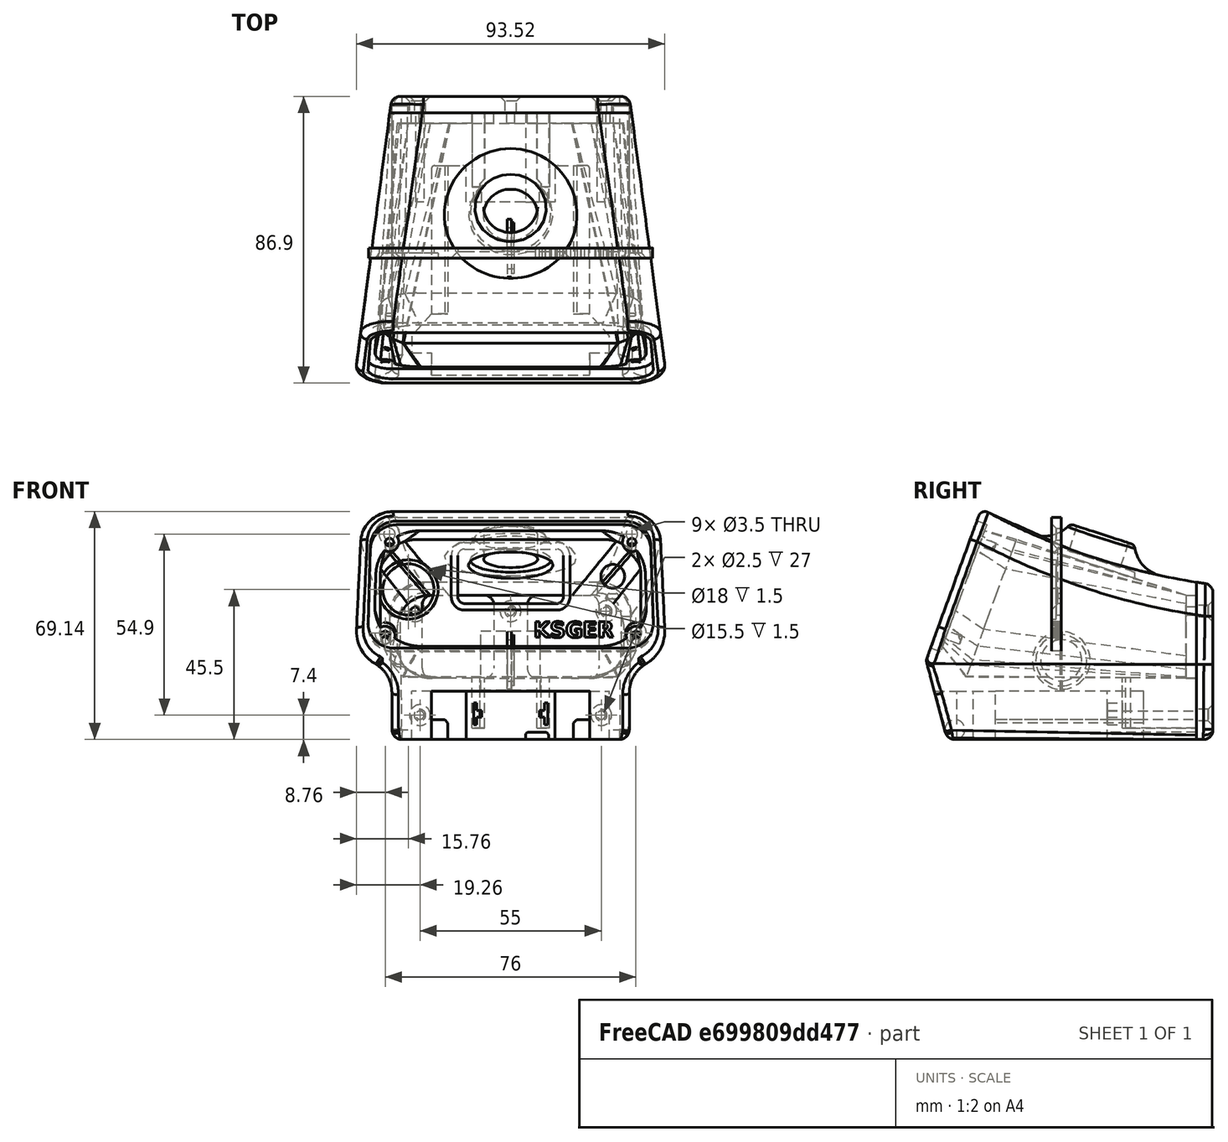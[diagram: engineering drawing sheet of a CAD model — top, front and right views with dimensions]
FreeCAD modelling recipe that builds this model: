
FCSTD DOCUMENT  (FreeCAD 2022.709R28846 (Git))
Label: solder_station5_snap_name
License: All rights reserved
LicenseURL: http://en.wikipedia.org/wiki/All_rights_reserved
objects: Sketcher::SketchObject×22, PartDesign::Pocket×12, Part::FeaturePython×6, PartDesign::Fillet×6, App::DocumentObjectGroup×4, PartDesign::Body×4, Mesh::Feature×4, PartDesign::Chamfer×3, PartDesign::FeatureBase×2, PartDesign::Pad×2, PartDesign::Revolution×2, Spreadsheet::Sheet×1, Part::Plane×1, Part::Loft×1, Part::Extrusion×1, Part::MultiCommon×1, Part::Box×1, PartDesign::SubtractiveLoft×1, PartDesign::Groove×1, Part::Part2DObjectPython×1, +2 more types
note: 124 computed .brp shape members not serialized (recipe doc carries the construction recipe); baked Part::Feature solids carry a one-line shape summary decoded from their .brp

FEATURE [Sketcher::SketchObject] Sketch  label="RearSupport"
  ArcFitTolerance = 0
  AttachmentOffset = pos=(0,0,-37.8) rot=(0,0,1;0rad)
  AttachmentSupport = -> [XZ_Plane005]
  FullyConstrained = true
  MapMode = 5
  Placement = pos=(0,37.8,8.4e-15) rot=(1,0,0;1.5708rad)
  Support = -> [XZ_Plane005]
  TreeRank = 0
  expr: AttachmentOffset.Base.z = -<<param>>.mid_depth / 2 + <<param>>.wall
  expr: Constraints[24] = 3
  expr: Constraints[37] = <<param>>.bottom_height
  expr: Constraints[38] = <<param>>.floor
  expr: Constraints[39] = <<param>>.rear_height - <<param>>.wall
  expr: Constraints[47] = <<param>>.reart_screw_width2
  expr: Constraints[48] = <<param>>.rear_screw_width1
  expr: Constraints[49] = <<param>>.screw_hole
  expr: Constraints[50] = <<param>>.rear_screw_height
  expr: Constraints[51] = <<param>>.rear_screw_height
  expr: Constraints[52] = <<param>>.rear_screw_offset
  sketch-geometry (22):
    g0: LineSegment StartX=-23.8 StartY=19.8 StartZ=0 EndX=-8.1 EndY=19.8 EndZ=0
    g1: LineSegment StartX=26.8 StartY=16.8 StartZ=0 EndX=26.8 EndY=-2.4 EndZ=0
    g2: LineSegment StartX=23.8 StartY=-5.4 StartZ=0 EndX=8.1 EndY=-5.4 EndZ=0
    g3: LineSegment StartX=-26.8 StartY=-2.4 StartZ=0 EndX=-26.8 EndY=16.8 EndZ=0
    g4: LineSegment StartX=-5.1 StartY=16.8 StartZ=0 EndX=-5.1 EndY=-2.4 EndZ=0
    g5: LineSegment StartX=5.1 StartY=16.8 StartZ=0 EndX=5.1 EndY=-2.4 EndZ=0
    g6: LineSegment StartX=8.1 StartY=19.8 StartZ=0 EndX=23.8 EndY=19.8 EndZ=0
    g7: LineSegment StartX=-8.1 StartY=-5.4 StartZ=0 EndX=-23.8 EndY=-5.4 EndZ=0
    g8: ArcOfCircle CenterX=-8.1 CenterY=16.8 CenterZ=0 NormalX=0 NormalY=0 NormalZ=1 AngleXU=0 Radius=3 StartAngle=0 EndAngle=1.5708
    g9: ArcOfCircle CenterX=8.1 CenterY=16.8 CenterZ=0 NormalX=0 NormalY=0 NormalZ=1 AngleXU=0 Radius=3 StartAngle=1.5708 EndAngle=3.14159
    g10: ArcOfCircle CenterX=-8.1 CenterY=-2.4 CenterZ=0 NormalX=0 NormalY=0 NormalZ=1 AngleXU=0 Radius=3 StartAngle=4.71239 EndAngle=6.28319
    g11: ArcOfCircle CenterX=8.1 CenterY=-2.4 CenterZ=0 NormalX=0 NormalY=0 NormalZ=1 AngleXU=0 Radius=3 StartAngle=3.14159 EndAngle=4.71239
    g12: ArcOfCircle CenterX=-23.8 CenterY=16.8 CenterZ=0 NormalX=0 NormalY=0 NormalZ=1 AngleXU=0 Radius=3 StartAngle=1.5708 EndAngle=3.14159
    g13: ArcOfCircle CenterX=-23.8 CenterY=-2.4 CenterZ=0 NormalX=0 NormalY=0 NormalZ=1 AngleXU=0 Radius=3 StartAngle=3.14159 EndAngle=4.71239
    g14: ArcOfCircle CenterX=23.8 CenterY=16.8 CenterZ=0 NormalX=0 NormalY=0 NormalZ=1 AngleXU=0 Radius=3 StartAngle=3e-16 EndAngle=1.5708
    g15: ArcOfCircle CenterX=23.8 CenterY=-2.4 CenterZ=0 NormalX=0 NormalY=0 NormalZ=1 AngleXU=0 Radius=3 StartAngle=4.71239 EndAngle=6.28319
    g16: Circle [constr] CenterX=0 CenterY=-24 CenterZ=0 NormalX=0 NormalY=0 NormalZ=1 AngleXU=0 Radius=3
    g17: Circle CenterX=0 CenterY=14.9 CenterZ=0 NormalX=0 NormalY=0 NormalZ=1 AngleXU=0 Radius=1.25
    g18: Circle CenterX=-29 CenterY=14.9 CenterZ=0 NormalX=0 NormalY=0 NormalZ=1 AngleXU=0 Radius=1.25
    g19: Circle [constr] CenterX=-27.5 CenterY=-16.6 CenterZ=0 NormalX=0 NormalY=0 NormalZ=1 AngleXU=0 Radius=1.25
    g20: Circle [constr] CenterX=27.5 CenterY=-16.6 CenterZ=0 NormalX=0 NormalY=0 NormalZ=1 AngleXU=0 Radius=1.25
    g21: Circle CenterX=29 CenterY=14.9 CenterZ=0 NormalX=0 NormalY=0 NormalZ=1 AngleXU=0 Radius=1.25
  constraints (53):
    c: Horizontal(g0)
    c: Horizontal(g2)
    c: Vertical(g1)
    c: Vertical(g3)
    c: Vertical(g4)
    c: Vertical(g5)
    c: Tangent(g0,g6)
    c: Tangent(g2,g7)
    c: Tangent(g0,g8) = 1.5708
    c: Tangent(g4,g8) = 1.5708
    c: Tangent(g5,g9) = -1.5708
    c: Tangent(g6,g9) = 1.5708
    c: Tangent(g7,g10) = 1.5708
    c: Tangent(g4,g10) = 1.5708
    c: Tangent(g5,g11) = -1.5708
    c: Tangent(g2,g11) = 1.5708
    c: Tangent(g0,g12) = 1.5708
    c: Tangent(g3,g12) = 1.5708
    c: Tangent(g3,g13) = 1.5708
    c: Tangent(g7,g13) = 1.5708
    c: Tangent(g6,g14) = 1.5708
    c: Tangent(g1,g14) = 1.5708
    c: Tangent(g1,g15) = 1.5708
    c: Tangent(g2,g15) = 1.5708
    c: Radius(g9) = 3
    c: Equal(g12,g13)
    c: Equal(g13,g10)
    c: Equal(g10,g8)
    c: Equal(g11,g15)
    c: Equal(g15,g14)
    c: Equal(g14,g9)
    c: DistanceX(g4,g-1) = 5.1
    c: DistanceX(g5,g1) = 21.7
    c: Symmetric(g4,g5,g-2)
    c: Equal(g7,g2)
    c: PointOnObject(g16,g-2)
    c: Radius(g16) = 3
    c: DistanceY(g16,g-1) = 24
    c: DistanceY(g16,g2) = 18.6
    c: DistanceY(g16,g6) = 43.8
    c: PointOnObject(g17,g-2)
    c: Equal(g21,g18)
    c: Equal(g18,g19)
    c: Equal(g19,g20)
    c: Equal(g18,g17)
    c: Symmetric(g20,g19,g-2)
    c: Symmetric(g18,g21,g-2)
    c: DistanceX(g19,g20) = 55
    c: DistanceX(g18,g21) = 58
    c: Diameter(g19) = 2.5
    c: DistanceY(g20,g21) = 31.5
    c: DistanceY(g20,g17) = 31.5
    c: DistanceY(g16,g19) = 7.4
FEATURE [Spreadsheet::Sheet] Spreadsheet  label="param"
  PythonMode = false
  ShowCells = 0
  TreeRank = 0
  cells = A1=Body; B2=top_depth; C2(top_depth)=70; B3=mid_depth; C3(mid_depth)=82; D3=half is rear reference; B4=bottom_depth; C4(bottom_depth)=75; B6=bottom_width; C6(bottom_width)=72; B7=bottom_height; C7(bottom_height)=24; B8=bottom_angle; C8(bottom_angle)=15; B10=rear_width; C10(rear_width)=72; B11=rear_height; C11(rear_height)=47; F11=41; B13=mid_width; C13(mid_width)=80; B14=mid_height; C14(mid_height)=56; F14=50; B16=front_width1; C16(front_width1)=92; D16=@top; E16=upper; F16=91; B17=front_width2; C17(front_width2)=95; D17=@mid; E17=lower; F17=94; B18=front_height; C18(front_height)=70; F18=64; B19=front_angle; C19(front_angle)=20; B21=wall; C21(wall)=3.2; B22=radius_big; C22(radius_big)=10; B23=radius_small; C23(radius_small)=3; B24=arch; C24(arch)=200; A26=Button; B27=button_offset; C27(button_offset)=10; B28=button_inside_dia; C28(button_inside_dia)=20; B29=button_outside_dia; C29(button_outside_dia)=22; B30=button_height; C30(button_height)=30.6; F30=26; B31=button_extension; C31(button_extension)=8; B32=button_fillet; C32(button_fillet)=12; B33=button_angle; C33(button_angle)=-18; F33=-17; B34=button_hole; C34(button_hole)=16.4; B35=button_hole_center; C35(button_hole_center)=-0.5; A37=Battery Cuts; B38=batt_carveout; C38(batt_carveout)=14.6; B39=batt_rail; C39(batt_rail)=6; B40=batt_rail_length; C40(batt_rail_length)=45; A42=Terminals; B43=terminal_height; C43(terminal_height)=6.6; B44=terminal_thickness; C44(terminal_thickness)=1; B45=terminal_seperation; C45(terminal_seperation)=21.5; B46=terminal_offset; C46(terminal_offset)=4.5; B47=terminal_depth; C47(terminal_depth)=22.5; A49=Box Interior; B50=floor; C50(floor)=18.6; B51=rear_inside_width; C51(rear_inside_width)==C10 - C21; D51=calc; B52=rear_inside_height; C52(rear_inside_height)==C11 - C21; D52=calc; B53=mid_inside_width; C53(mid_inside_width)==C13; D53=calc; B54=mid_inside_height; C54(mid_inside_height)==C14 + 7; D54=calc; F54=6; B55=front_inside_width1; C55(front_inside_width1)==C62 - C58 * 2; D55=calc; E55=upper; B56=front_inside_width2; C56(front_inside_width2)==C63 - C58 * 2; D56=calc; E56=lower; B57=front_inside_height; C57(front_inside_height)==C64 - C59 * 2; D57=calc; B58=front_width_lip_width; C58(front_width_lip_width)=3; B59=front_inside_lip_height; C59(front_inside_lip_height)=2; A61=Face; B62=face_width1; C62(face_width1)==84 + 1; B63=face_width2; C63(face_width2)==85.5 + 1; B64=face_height; C64(face_height)=41; F64=35; B65=face_thickness; C65(face_thickness)=3; B66=face_radius; C66(face_radius)=8; B67=face_offset; C67(face_offset)=2.8; F67=2.8; A69=Screws; B70=screw_hole; C70(screw_hole)=2.5; B72=front_screw_width1; C72(front_screw_width1)=73.5; D72=upper; B73=front_screw_width2; C73(front_screw_width2)=76; D73=lower; B74=front_screw_height; C74(front_screw_height)=30; F74=24; B75=front_screw_offset; C75(front_screw_offset)=5.5; B77=rear_screw_width1; C77(rear_screw_width1)=58; B78=reart_screw_width2; C78(reart_screw_width2)=55; B79=rear_screw_height; C79(rear_screw_height)=31.5; F79=25.5; B80=rear_screw_offset; C80(rear_screw_offset)=7.4; A82=Back; B83=back_thickness; C83(back_thickness)=5
FEATURE [Sketcher::SketchObject] Sketch008  label="SketchButtonHole"
  ArcFitTolerance = 0
  AttachmentOffset = pos=(0,-0.5,30.6) rot=(1,0,0;-0.314159rad)
  AttachmentSupport = -> [XY_Plane005]
  FullyConstrained = true
  MapMode = 5
  Placement = pos=(0,-0.5,30.6) rot=(1,0,0;5.96903rad)
  Support = -> [XY_Plane005]
  TreeRank = 0
  expr: AttachmentOffset.Base.y = <<param>>.button_hole_center
  expr: AttachmentOffset.Base.z = <<param>>.button_height
  expr: AttachmentOffset.Rotation.Angle = <<param>>.button_angle
  expr: Constraints[0] = <<param>>.button_hole
  expr: Constraints[2] = <<param>>.button_offset
  sketch-geometry (1):
    g0: Circle CenterX=0 CenterY=10 CenterZ=0 NormalX=0 NormalY=0 NormalZ=1 AngleXU=0 Radius=8.2
  constraints (3):
    c: Diameter(g0) = 16.4
    c: PointOnObject(g0,g-2)
    c: DistanceY(g-1,g0) = 10
FEATURE [Sketcher::SketchObject] Sketch012  label="SketchSide"
  ArcFitTolerance = 0
  AttachmentOffset = pos=(2.5,0,0) rot=(0,0,1;0rad)
  AttachmentSupport = -> [YZ_Plane006]
  FullyConstrained = true
  MapMode = 5
  Placement = pos=(6e-16,2.5,-6e-16) rot=(0.57735,0.57735,0.57735;2.0944rad)
  Support = -> [YZ_Plane006]
  TreeRank = 0
  expr: AttachmentOffset.Base.x = <<param>>.back_thickness / 2
  expr: Constraints[14] = <<param>>.bottom_height
  expr: Constraints[15] = <<param>>.radius_small
  expr: Constraints[16] = 90 - <<param>>.bottom_angle
  expr: Constraints[17] = 90 - <<param>>.front_angle
  expr: Constraints[21] = <<param>>.front_height
  expr: Constraints[4] = <<param>>.rear_height - <<param>>.bottom_height
  expr: Constraints[5] = <<param>>.arch
  expr: Constraints[6] = <<param>>.mid_depth + <<param>>.back_thickness
  sketch-geometry (7):
    g0: LineSegment StartX=43.5 StartY=0 StartZ=0 EndX=43.5 EndY=23 EndZ=0
    g1: LineSegment StartX=-43.5 StartY=0 StartZ=0 EndX=-26.7574 EndY=46 EndZ=0
    g2: ArcOfCircle CenterX=69.5235 CenterY=221.3 CenterZ=0 NormalX=0 NormalY=0 NormalZ=1 AngleXU=0 Radius=200 StartAngle=4.21013 EndAngle=4.5819
    g3: LineSegment StartX=-43.5 StartY=0 StartZ=0 EndX=-37.665 EndY=-21.7765 EndZ=0
    g4: LineSegment StartX=-34.7673 StartY=-24 StartZ=0 EndX=43.5 EndY=-24 EndZ=0
    g5: LineSegment StartX=43.5 StartY=-24 StartZ=0 EndX=43.5 EndY=0 EndZ=0
    g6: ArcOfCircle CenterX=-34.7672 CenterY=-21 CenterZ=0 NormalX=0 NormalY=0 NormalZ=1 AngleXU=0 Radius=3 StartAngle=3.4034 EndAngle=4.71238
  constraints (22):
    c: PointOnObject(g1,g-1)
    c: Vertical(g0)
    c: Coincident(g2,g0)
    c: Symmetric(g1,g0,g-2)
    c: DistanceY(g0,g0) = 23
    c: Radius(g2) = 200
    c: DistanceX(g1,g0) = 87
    c: Horizontal(g4)
    c: Coincident(g5,g4)
    c: Vertical(g5)
    c: Coincident(g6,g3)
    c: Coincident(g6,g4)
    c: Tangent(g6,g4)
    c: Tangent(g6,g3)
    c: DistanceY(g4,g-1) = 24
    c: Radius(g6) = 3
    c: Angle(g3,g-1) = 1.309
    c: Angle(g-1,g1) = 1.22173
    c: Coincident(g3,g1)
    c: Coincident(g5,g0)
    c: Coincident(g2,g1)
    c: DistanceY(g4,g1) = 70
FEATURE [Sketcher::SketchObject] Sketch018  label="SketchBat1"
  ArcFitTolerance = 0
  AttachmentOffset = pos=(0,0,-24) rot=(0,0,1;0rad)
  AttachmentSupport = -> [XY_Plane005]
  FullyConstrained = true
  MapMode = 5
  Placement = pos=(0,0,-24) rot=(0,0,1;0rad)
  Support = -> [XY_Plane005]
  TreeRank = 0
  expr: AttachmentOffset.Base.z = -<<param>>.bottom_height
  expr: Constraints[63] = <<param>>.batt_rail_length
  expr: Constraints[64] = <<param>>.mid_depth / 2
  sketch-geometry (21):
    g0: LineSegment StartX=-24 StartY=-41.7082 StartZ=0 EndX=24 EndY=-41.7082 EndZ=0
    g1: LineSegment StartX=24 StartY=-41.7082 StartZ=0 EndX=24 EndY=-31.7082 EndZ=0
    g2: LineSegment StartX=24 StartY=-31.7082 StartZ=0 EndX=30 EndY=-31.7082 EndZ=0
    g3: LineSegment StartX=30 StartY=-31.7082 StartZ=0 EndX=30 EndY=-26.7082 EndZ=0
    g4: LineSegment StartX=30 StartY=-26.7082 StartZ=0 EndX=24 EndY=-20 EndZ=0
    g5: LineSegment StartX=24 StartY=-20 StartZ=0 EndX=24 EndY=24 EndZ=0
    g6: LineSegment StartX=13.5 StartY=24 StartZ=0 EndX=13.5 EndY=14 EndZ=0
    g7: LineSegment StartX=13.5 StartY=14 StartZ=0 EndX=-13.5 EndY=14 EndZ=0
    g8: LineSegment StartX=-13.5 StartY=14 StartZ=0 EndX=-13.5 EndY=24 EndZ=0
    g9: LineSegment StartX=-24 StartY=24 StartZ=0 EndX=-24 EndY=-20 EndZ=0
    g10: LineSegment StartX=-24 StartY=-20 StartZ=0 EndX=-30 EndY=-26.7082 EndZ=0
    g11: LineSegment StartX=-30 StartY=-26.7082 StartZ=0 EndX=-30 EndY=-31.7082 EndZ=0
    g12: LineSegment StartX=-30 StartY=-31.7082 StartZ=0 EndX=-24 EndY=-31.7082 EndZ=0
    g13: LineSegment StartX=-24 StartY=-31.7082 StartZ=0 EndX=-24 EndY=-41.7082 EndZ=0
    g14: Circle [constr] CenterX=0 CenterY=41 CenterZ=0 NormalX=0 NormalY=0 NormalZ=1 AngleXU=0 Radius=4
    g15: ArcOfCircle CenterX=-14.5 CenterY=24 CenterZ=0 NormalX=0 NormalY=0 NormalZ=1 AngleXU=0 Radius=1 StartAngle=6.28318 EndAngle=7.85399
    g16: LineSegment StartX=-23 StartY=25 StartZ=0 EndX=-14.5 EndY=25 EndZ=0
    g17: LineSegment StartX=14.5 StartY=25 StartZ=0 EndX=23 EndY=25 EndZ=0
    g18: ArcOfCircle CenterX=-23 CenterY=24 CenterZ=0 NormalX=0 NormalY=0 NormalZ=1 AngleXU=0 Radius=1 StartAngle=1.57079 EndAngle=3.1416
    g19: ArcOfCircle CenterX=14.5 CenterY=24 CenterZ=0 NormalX=0 NormalY=0 NormalZ=1 AngleXU=0 Radius=1 StartAngle=1.5708 EndAngle=3.14159
    g20: ArcOfCircle CenterX=23 CenterY=24 CenterZ=0 NormalX=0 NormalY=0 NormalZ=1 AngleXU=0 Radius=1.00001 StartAngle=2.75124e-06 EndAngle=1.5708
  constraints (65):
    c: Horizontal(g0)
    c: Coincident(g1,g0)
    c: Vertical(g1)
    c: Coincident(g2,g1)
    c: Horizontal(g2)
    c: Coincident(g3,g2)
    c: Coincident(g3,g4)
    c: Vertical(g5)
    c: Coincident(g6,g7)
    c: Coincident(g7,g8)
    c: Vertical(g8)
    c: Vertical(g9)
    c: Coincident(g10,g11)
    c: Vertical(g11)
    c: Coincident(g11,g12)
    c: Horizontal(g12)
    c: Coincident(g12,g13)
    c: Equal(g6,g8)
    c: Equal(g5,g9)
    c: Equal(g4,g10)
    c: Equal(g3,g11)
    c: Equal(g12,g2)
    c: Equal(g1,g13)
    c: Coincident(g13,g0)
    c: Vertical(g13)
    c: DistanceX(g7,g7) = 27
    c: Symmetric(g7,g6,g-2)
    c: Distance(g4) = 9
    c: Vertical(g3)
    c: DistanceY(g3,g3) = 5
    c: DistanceX(g2,g2) = 6
    c: DistanceY(g1,g1) = 10
    c: DistanceX(g0,g0) = 48
    c: PointOnObject(g14,g-2)
    c: Coincident(g9,g10)
    c: Coincident(g5,g4)
    c: Coincident(g15,g8)
    c: Coincident(g16,g15)
    c: Tangent(g15,g8)
    c: Horizontal(g16)
    c: Horizontal(g17)
    c: DistanceX(g9,g5) = 48
    c: Symmetric(g4,g9,g-2)
    c: Equal(g16,g17)
    c: Coincident(g18,g9)
    c: Coincident(g18,g16)
    c: Equal(g18,g15)
    c: Tangent(g18,g16)
    c: Tangent(g18,g9)
    c: DistanceY(g6,g17) = 11
    c: Vertical(g6)
    c: Coincident(g19,g6)
    c: Coincident(g19,g17)
    c: Coincident(g20,g17)
    c: Coincident(g20,g5)
    c: Tangent(g20,g17)
    c: Tangent(g20,g5)
    c: Tangent(g19,g6)
    c: Tangent(g19,g17)
    c: Equal(g15,g19)
    c: Radius(g19) = 1
    c: Radius(g14) = 4
    c: DistanceY(g15,g14) = 16
    c: DistanceY(g9,g16) = 45
    c: DistanceY(g-1,g14) = 41
FEATURE [Sketcher::SketchObject] Sketch019  label="SketchBat2"
  ArcFitTolerance = 0
  AttachmentOffset = pos=(0,0,-25) rot=(0,0,1;0rad)
  AttachmentSupport = -> [XZ_Plane005]
  FullyConstrained = true
  MapMode = 5
  Placement = pos=(0,25,5.6e-15) rot=(1,0,0;1.5708rad)
  Support = -> [XZ_Plane005]
  TreeRank = 0
  expr: AttachmentOffset.Base.z = -<<param>>.mid_depth / 2 + 16
  expr: Constraints[17] = <<param>>.bottom_height
  expr: Constraints[18] = <<param>>.batt_rail
  expr: Constraints[19] = 48.01mm
  sketch-geometry (10):
    g0: LineSegment StartX=-24.005 StartY=-18 StartZ=0 EndX=-20.005 EndY=-18 EndZ=0
    g1: LineSegment StartX=-19.005 StartY=-24 StartZ=0 EndX=-24.005 EndY=-24 EndZ=0
    g2: LineSegment StartX=-24.005 StartY=-24 StartZ=0 EndX=-24.005 EndY=-18 EndZ=0
    g3: LineSegment StartX=24.005 StartY=-18 StartZ=0 EndX=20.005 EndY=-18 EndZ=0
    g4: LineSegment StartX=19.005 StartY=-24 StartZ=0 EndX=24.005 EndY=-24 EndZ=0
    g5: LineSegment StartX=24.005 StartY=-24 StartZ=0 EndX=24.005 EndY=-18 EndZ=0
    g6: LineSegment StartX=-19.005 StartY=-19 StartZ=0 EndX=-19.005 EndY=-24 EndZ=0
    g7: LineSegment StartX=19.005 StartY=-24 StartZ=0 EndX=19.005 EndY=-19 EndZ=0
    g8: LineSegment StartX=-20.005 StartY=-18 StartZ=0 EndX=-19.005 EndY=-19 EndZ=0
    g9: LineSegment StartX=19.005 StartY=-19 StartZ=0 EndX=20.005 EndY=-18 EndZ=0
  constraints (29):
    c: Coincident(g1,g2)
    c: Coincident(g2,g0)
    c: Horizontal(g0)
    c: Horizontal(g1)
    c: Vertical(g2)
    c: Coincident(g4,g5)
    c: Coincident(g5,g3)
    c: Horizontal(g3)
    c: Horizontal(g4)
    c: Vertical(g5)
    c: Coincident(g6,g1)
    c: Vertical(g6)
    c: Equal(g1,g4)
    c: Coincident(g7,g4)
    c: Vertical(g7)
    c: Equal(g6,g7)
    c: Symmetric(g1,g4,g-2)
    c: DistanceY(g1,g-1) = 24
    c: DistanceY(g4,g3) = 6
    c: DistanceX(g1,g4) = 48.01
    c: DistanceX(g4,g4) = 5
    c: Coincident(g8,g0)
    c: Coincident(g8,g6)
    c: Coincident(g9,g7)
    c: Coincident(g9,g3)
    c: Equal(g0,g3)
    c: Equal(g2,g5)
    c: DistanceX(g0,g0) = 4
    c: DistanceY(g1,g6) = 5
FEATURE [Sketcher::SketchObject] Sketch021  label="SketchButton"
  ArcFitTolerance = 0
  AttachmentOffset = pos=(10,30.6,0) rot=(0,0,1;-0.314159rad)
  AttachmentSupport = -> [YZ_Plane005]
  FullyConstrained = true
  MapMode = 5
  Placement = pos=(-4.6e-15,10,30.6) rot=(-0.506732,-0.697457,-0.506732;4.35963rad)
  Support = -> [YZ_Plane005]
  TreeRank = 0
  expr: AttachmentOffset.Base.x = <<param>>.button_offset
  expr: AttachmentOffset.Base.y = <<param>>.button_height
  expr: AttachmentOffset.Rotation.Angle = <<param>>.button_angle
  expr: Constraints[6] = <<param>>.button_extension
  expr: Constraints[7] = <<param>>.button_outside_dia / 2
  sketch-geometry (5):
    g0: LineSegment StartX=0 StartY=0 StartZ=0 EndX=0 EndY=8 EndZ=0
    g1: LineSegment StartX=0 StartY=8 StartZ=0 EndX=9 EndY=8 EndZ=0
    g2: LineSegment StartX=0 StartY=0 StartZ=0 EndX=11 EndY=0 EndZ=0
    g3: LineSegment StartX=11 StartY=0 StartZ=0 EndX=11 EndY=6 EndZ=0
    g4: ArcOfCircle CenterX=9 CenterY=6 CenterZ=0 NormalX=0 NormalY=0 NormalZ=1 AngleXU=0 Radius=2 StartAngle=1e-16 EndAngle=1.5708
  constraints (13):
    c: Coincident(g0,g-1)
    c: PointOnObject(g0,g-2)
    c: Coincident(g1,g0)
    c: Horizontal(g1)
    c: Coincident(g2,g0)
    c: Horizontal(g2)
    c: DistanceY(g0,g0) = 8
    c: DistanceX(g2,g2) = 11
    c: Coincident(g3,g2)
    c: Vertical(g3)
    c: Radius(g4) = 2
    c: Tangent(g4,g1) = 1.5708
    c: Tangent(g4,g3) = -1.5708
FEATURE [Sketcher::SketchObject] Sketch022  label="SketchRearInside"
  ArcFitTolerance = 0
  AttachmentOffset = pos=(0,0,-37.8) rot=(0,0,1;0rad)
  AttachmentSupport = -> [XZ_Plane005]
  FullyConstrained = true
  MapMode = 5
  Placement = pos=(0,37.8,8.4e-15) rot=(1,0,0;1.5708rad)
  Support = -> [XZ_Plane005]
  TreeRank = 0
  expr: AttachmentOffset.Base.z = -<<param>>.mid_depth / 2 + <<param>>.wall
  expr: Constraints[12] = <<param>>.radius_big
  expr: Constraints[18] = <<param>>.rear_inside_width
  expr: Constraints[26] = <<param>>.bottom_height
  expr: Constraints[27] = <<param>>.rear_inside_height
  expr: Constraints[29] = <<param>>.floor
  sketch-geometry (9):
    g0: LineSegment StartX=-34.4 StartY=9.80003 StartZ=0 EndX=-34.4 EndY=4.59997 EndZ=0
    g1: LineSegment StartX=-24.4 StartY=-5.4 StartZ=0 EndX=24.4 EndY=-5.4 EndZ=0
    g2: LineSegment StartX=34.4 StartY=4.59997 StartZ=0 EndX=34.4 EndY=9.80003 EndZ=0
    g3: LineSegment StartX=-24.4 StartY=19.8 StartZ=0 EndX=24.4 EndY=19.8 EndZ=0
    g4: ArcOfCircle CenterX=24.4 CenterY=9.8 CenterZ=0 NormalX=0 NormalY=0 NormalZ=1 AngleXU=0 Radius=10 StartAngle=3.49027e-06 EndAngle=1.57079
    g5: ArcOfCircle CenterX=24.4 CenterY=4.6 CenterZ=0 NormalX=0 NormalY=0 NormalZ=1 AngleXU=0 Radius=10 StartAngle=4.71239 EndAngle=6.28318
    g6: ArcOfCircle CenterX=-24.4 CenterY=9.8 CenterZ=0 NormalX=0 NormalY=0 NormalZ=1 AngleXU=0 Radius=10 StartAngle=1.5708 EndAngle=3.14159
    g7: ArcOfCircle CenterX=-24.4 CenterY=4.6 CenterZ=0 NormalX=0 NormalY=0 NormalZ=1 AngleXU=0 Radius=10 StartAngle=3.1416 EndAngle=4.71239
    g8: Circle [constr] CenterX=0 CenterY=-24 CenterZ=0 NormalX=0 NormalY=0 NormalZ=1 AngleXU=0 Radius=3
  constraints (30):
    c: Vertical(g0)
    c: Horizontal(g1)
    c: Vertical(g2)
    c: Horizontal(g3)
    c: Equal(g3,g1)
    c: Equal(g0,g2)
    c: Coincident(g4,g3)
    c: Coincident(g4,g2)
    c: Coincident(g5,g2)
    c: Coincident(g5,g1)
    c: Coincident(g6,g0)
    c: Coincident(g6,g3)
    c: Radius(g6) = 10
    c: Equal(g6,g4)
    c: Equal(g4,g5)
    c: Coincident(g7,g1)
    c: Coincident(g7,g0)
    c: Equal(g5,g7)
    c: DistanceX(g0,g2) = 68.8
    c: Symmetric(g0,g2,g-2)
    c: Tangent(g4,g2)
    c: Tangent(g4,g3)
    c: Tangent(g5,g2)
    c: Tangent(g5,g1)
    c: Tangent(g6,g3)
    c: PointOnObject(g8,g-2)
    c: DistanceY(g8,g-1) = 24
    c: DistanceY(g8,g3) = 43.8
    c: Radius(g8) = 3
    c: DistanceY(g8,g1) = 18.6
FEATURE [Sketcher::SketchObject] Sketch024  label="SketchFaceCut"
  ArcFitTolerance = 0
  AttachmentOffset = pos=(0,0,37.6) rot=(1,0,0;-0.349066rad)
  AttachmentSupport = -> [XZ_Plane005]
  FullyConstrained = true
  MapMode = 5
  Placement = pos=(0,-37.6,-8.3e-15) rot=(-1,0,0;5.06145rad)
  Support = -> [XZ_Plane005]
  TreeRank = 0
  expr: AttachmentOffset.Base.z = <<param>>.mid_depth / 2 - <<param>>.face_thickness - 0.4
  expr: AttachmentOffset.Rotation.Angle = -<<param>>.front_angle
  expr: Constraints[13] = <<param>>.face_radius
  expr: Constraints[22] = <<param>>.face_width1
  expr: Constraints[23] = <<param>>.face_width2
  expr: Constraints[24] = <<param>>.face_offset
  expr: Constraints[25] = <<param>>.face_height
  sketch-geometry (8):
    g0: LineSegment StartX=-34.5035 StartY=43.8 StartZ=0 EndX=34.5037 EndY=43.8 EndZ=0
    g1: LineSegment StartX=42.5001 StartY=36.0399 StartZ=0 EndX=43.25 EndY=11.0399 EndZ=0
    g2: LineSegment StartX=35.2536 StartY=2.8 StartZ=0 EndX=-35.2536 EndY=2.8 EndZ=0
    g3: LineSegment StartX=-43.25 StartY=11.0399 StartZ=0 EndX=-42.4999 EndY=36.0399 EndZ=0
    g4: ArcOfCircle CenterX=34.5037 CenterY=35.8 CenterZ=0 NormalX=0 NormalY=0 NormalZ=1 AngleXU=0 Radius=8 StartAngle=0.0299879 EndAngle=1.5708
    g5: ArcOfCircle CenterX=35.2536 CenterY=10.8 CenterZ=0 NormalX=0 NormalY=0 NormalZ=1 AngleXU=0 Radius=8 StartAngle=4.71239 EndAngle=6.31317
    g6: ArcOfCircle CenterX=-34.5035 CenterY=35.8 CenterZ=0 NormalX=0 NormalY=0 NormalZ=1 AngleXU=0 Radius=8 StartAngle=1.5708 EndAngle=3.1116
    g7: ArcOfCircle CenterX=-35.2536 CenterY=10.8 CenterZ=0 NormalX=0 NormalY=0 NormalZ=1 AngleXU=0 Radius=8 StartAngle=3.1116 EndAngle=4.71239
  constraints (27):
    c: Horizontal(g0)
    c: Coincident(g4,g0)
    c: Coincident(g4,g1)
    c: Coincident(g5,g1)
    c: Coincident(g5,g2)
    c: Coincident(g6,g0)
    c: Coincident(g6,g3)
    c: Coincident(g7,g3)
    c: Coincident(g7,g2)
    c: Equal(g1,g3)
    c: Equal(g4,g6)
    c: Equal(g6,g7)
    c: Equal(g7,g5)
    c: Radius(g4) = 8
    c: Tangent(g6,g3)
    c: Tangent(g7,g3)
    c: Tangent(g7,g2)
    c: Tangent(g6,g0)
    c: Tangent(g4,g0)
    c: Tangent(g4,g1)
    c: Tangent(g5,g1)
    c: Tangent(g5,g2)
    c: DistanceX(g3,g1) = 85
    c: DistanceX(g3,g1) = 86.5
    c: DistanceY(g-1,g2) = 2.8
    c: DistanceY(g2,g0) = 41
    c: Symmetric(g2,g2,g-2)
FEATURE [Sketcher::SketchObject] Sketch025  label="SketchMidInside"
  ArcFitTolerance = 0
  AttachmentOffset = pos=(0,0,27) rot=(1,0,0;-0.349066rad)
  AttachmentSupport = -> [XZ_Plane005]
  FullyConstrained = true
  MapMode = 5
  Placement = pos=(0,-27,-6e-15) rot=(-1,0,0;5.06145rad)
  Support = -> [XZ_Plane005]
  TreeRank = 0
  expr: AttachmentOffset.Base.z = <<param>>.mid_depth / 2 - 14
  expr: AttachmentOffset.Rotation.Angle = -<<param>>.front_angle
  expr: Constraints[10] = <<param>>.radius_big + 1
  expr: Constraints[11] = <<param>>.floor
  expr: Constraints[12] = Spreadsheet.mid_inside_width - 1
  expr: Constraints[14] = <<param>>.mid_inside_height
  expr: Constraints[23] = <<param>>.mid_width - 15
  expr: Constraints[4] = <<param>>.bottom_height
  sketch-geometry (9):
    g0: LineSegment StartX=-28.5 StartY=39 StartZ=0 EndX=28.5 EndY=39 EndZ=0
    g1: LineSegment StartX=39.5 StartY=28 StartZ=0 EndX=39.5 EndY=10 EndZ=0
    g2: LineSegment StartX=32.5 StartY=-5.4 StartZ=0 EndX=-32.5 EndY=-5.4 EndZ=0
    g3: LineSegment StartX=-39.5 StartY=10 StartZ=0 EndX=-39.5 EndY=28 EndZ=0
    g4: Circle [constr] CenterX=0 CenterY=-24 CenterZ=0 NormalX=0 NormalY=0 NormalZ=1 AngleXU=0 Radius=3
    g5: ArcOfCircle CenterX=-28.5 CenterY=28 CenterZ=0 NormalX=0 NormalY=0 NormalZ=1 AngleXU=0 Radius=11 StartAngle=1.5708 EndAngle=3.14159
    g6: ArcOfCircle CenterX=28.5 CenterY=28 CenterZ=0 NormalX=0 NormalY=0 NormalZ=1 AngleXU=0 Radius=11 StartAngle=0 EndAngle=1.5708
    g7: ArcOfCircle CenterX=-15.553 CenterY=11.5941 CenterZ=0 NormalX=0 NormalY=0 NormalZ=1 AngleXU=0 Radius=24 StartAngle=3.20806 EndAngle=3.92838
    g8: ArcOfCircle CenterX=15.553 CenterY=11.5941 CenterZ=0 NormalX=0 NormalY=0 NormalZ=1 AngleXU=0 Radius=24 StartAngle=5.4964 EndAngle=6.21672
  constraints (25):
    c: Vertical(g1)
    c: Vertical(g3)
    c: PointOnObject(g4,g-2)
    c: Radius(g4) = 3
    c: DistanceY(g4,g-1) = 24
    c: Tangent(g3,g5) = 1.5708
    c: Tangent(g0,g5) = 1.5708
    c: Tangent(g0,g6) = 1.5708
    c: Tangent(g1,g6) = 1.5708
    c: Equal(g6,g5)
    c: Radius(g6) = 11
    c: DistanceY(g4,g2) = 18.6
    c: DistanceX(g3,g1) = 79
    c: Symmetric(g2,g2,g-2)
    c: DistanceY(g4,g0) = 63
    c: Symmetric(g0,g0,g-2)
    c: Equal(g3,g1)
    c: Coincident(g7,g2)
    c: Coincident(g8,g1)
    c: Coincident(g8,g2)
    c: Coincident(g7,g3)
    c: Equal(g8,g7)
    c: Radius(g8) = 24
    c: DistanceX(g2,g2) = 65
    c: DistanceY(g1,g1) = 18
FEATURE [Sketcher::SketchObject] Sketch026  label="SketchFrontScrews"
  ArcFitTolerance = 0
  AttachmentOffset = pos=(0,0,38) rot=(1,0,0;-0.349066rad)
  AttachmentSupport = -> [XZ_Plane005]
  FullyConstrained = true
  MapMode = 5
  Placement = pos=(0,-38,-8.4e-15) rot=(-1,0,0;5.06145rad)
  Support = -> [XZ_Plane005]
  TreeRank = 0
  expr: AttachmentOffset.Base.z = <<param>>.mid_depth / 2 - <<param>>.face_thickness
  expr: AttachmentOffset.Rotation.Angle = -<<param>>.front_angle
  expr: Constraints[0] = <<param>>.front_screw_width1
  expr: Constraints[13] = <<param>>.screw_hole
  expr: Constraints[1] = <<param>>.front_screw_width2
  expr: Constraints[2] = <<param>>.front_screw_height
  expr: Constraints[9] = <<param>>.face_offset + <<param>>.front_screw_offset
  sketch-geometry (6):
    g0: Circle CenterX=-36.75 CenterY=38.3 CenterZ=0 NormalX=0 NormalY=0 NormalZ=1 AngleXU=0 Radius=1.25
    g1: Circle CenterX=36.75 CenterY=38.3 CenterZ=0 NormalX=0 NormalY=0 NormalZ=1 AngleXU=0 Radius=1.25
    g2: Circle CenterX=-38 CenterY=8.3 CenterZ=0 NormalX=0 NormalY=0 NormalZ=1 AngleXU=0 Radius=1.25
    g3: Circle CenterX=38 CenterY=8.3 CenterZ=0 NormalX=0 NormalY=0 NormalZ=1 AngleXU=0 Radius=1.25
    g4: LineSegment [constr] StartX=-36.75 StartY=38.3 StartZ=0 EndX=36.75 EndY=38.3 EndZ=0
    g5: LineSegment [constr] StartX=-38 StartY=8.3 StartZ=0 EndX=38 EndY=8.3 EndZ=0
  constraints (14):
    c: DistanceX(g0,g1) = 73.5
    c: DistanceX(g2,g3) = 76
    c: DistanceY(g3,g1) = 30
    c: Coincident(g4,g0)
    c: Coincident(g4,g1)
    c: Coincident(g5,g2)
    c: Coincident(g5,g3)
    c: Symmetric(g2,g3,g-2)
    c: Symmetric(g0,g1,g-2)
    c: DistanceY(g-1,g3) = 8.3
    c: Equal(g0,g2)
    c: Equal(g2,g3)
    c: Equal(g3,g1)
    c: Diameter(g0) = 2.5
FEATURE [Sketcher::SketchObject] Sketch023  label="SketchFrontInside"
  ArcFitTolerance = 0
  AttachmentOffset = pos=(0,0,38) rot=(1,0,0;-0.349066rad)
  AttachmentSupport = -> [XZ_Plane005]
  ExternalGeometry = -> [Sketch026,Sketch024]
  FullyConstrained = true
  MapMode = 5
  Placement = pos=(0,-38,-8.4e-15) rot=(-1,0,0;5.06145rad)
  Support = -> [XZ_Plane005]
  TreeRank = 0
  expr: AttachmentOffset.Base.z = <<param>>.mid_depth / 2 - <<param>>.face_thickness
  expr: AttachmentOffset.Rotation.Angle = -<<param>>.front_angle
  sketch-geometry (16):
    g0: LineSegment StartX=-27.5 StartY=4.93681 StartZ=0 EndX=27.5 EndY=4.93681 EndZ=0
    g1: LineSegment StartX=27.5 StartY=41.9368 StartZ=0 EndX=-27.5 EndY=41.9368 EndZ=0
    g2: LineSegment StartX=-40.95 StartY=28.0001 StartZ=0 EndX=-41.25 EndY=18.0001 EndZ=0
    g3: LineSegment StartX=40.95 StartY=28 StartZ=0 EndX=41.25 EndY=18 EndZ=0
    g4: ArcOfCircle CenterX=36.75 CenterY=38.3 CenterZ=0 NormalX=0 NormalY=0 NormalZ=1 AngleXU=0 Radius=3 StartAngle=2.46996 EndAngle=5.23357
    g5: ArcOfCircle CenterX=27.5 CenterY=27.5965 CenterZ=0 NormalX=0 NormalY=0 NormalZ=1 AngleXU=0 Radius=13.4561 StartAngle=0.0299886 EndAngle=0.646116
    g6: ArcOfCircle CenterX=27.5 CenterY=27.5965 CenterZ=0 NormalX=0 NormalY=0 NormalZ=1 AngleXU=0 Radius=14.3403 StartAngle=1.06869 EndAngle=1.5708
    g7: ArcOfCircle CenterX=38 CenterY=8.3 CenterZ=0 NormalX=0 NormalY=0 NormalZ=1 AngleXU=0 Radius=3 StartAngle=1.04133 EndAngle=3.41706
    g8: ArcOfCircle CenterX=27.5 CenterY=17.5875 CenterZ=0 NormalX=0 NormalY=0 NormalZ=1 AngleXU=0 Radius=13.7562 StartAngle=5.77461 EndAngle=6.31317
    g9: ArcOfCircle CenterX=27.5 CenterY=17.5875 CenterZ=0 NormalX=0 NormalY=0 NormalZ=1 AngleXU=0 Radius=12.6507 StartAngle=4.71239 EndAngle=5.35813
    g10: ArcOfCircle CenterX=-36.75 CenterY=38.3 CenterZ=0 NormalX=0 NormalY=0 NormalZ=1 AngleXU=0 Radius=3 StartAngle=4.19123 EndAngle=6.95482
    g11: ArcOfCircle CenterX=-27.5 CenterY=27.5965 CenterZ=0 NormalX=0 NormalY=0 NormalZ=1 AngleXU=0 Radius=13.456 StartAngle=2.49548 EndAngle=3.1116
    g12: ArcOfCircle CenterX=-27.5 CenterY=27.5965 CenterZ=0 NormalX=0 NormalY=0 NormalZ=1 AngleXU=0 Radius=14.3403 StartAngle=1.5708 EndAngle=2.0729
    g13: ArcOfCircle CenterX=-38 CenterY=8.3 CenterZ=0 NormalX=0 NormalY=0 NormalZ=1 AngleXU=0 Radius=3 StartAngle=6.00771 EndAngle=8.38345
    g14: ArcOfCircle CenterX=-27.5 CenterY=17.5875 CenterZ=0 NormalX=0 NormalY=0 NormalZ=1 AngleXU=0 Radius=13.7562 StartAngle=3.1116 EndAngle=3.65016
    g15: ArcOfCircle CenterX=-27.5 CenterY=17.5875 CenterZ=0 NormalX=0 NormalY=0 NormalZ=1 AngleXU=0 Radius=12.6507 StartAngle=4.06665 EndAngle=4.71239
  constraints (42):
    c: Symmetric(g0,g0,g-2)
    c: Symmetric(g1,g1,g-2)
    c: DistanceY(g3,g3) = 10
    c: Equal(g3,g2)
    c: Equal(g1,g0)
    c: DistanceX(g1,g1) = 55
    c: Coincident(g4,g-3)
    c: Coincident(g5,g4)
    c: Coincident(g6,g4)
    c: Radius(g4) = 3
    c: Tangent(g5,g3) = 1.5708
    c: Parallel(g3,g-8)
    c: Tangent(g6,g1) = -1.5708
    c: DistanceX(g3,g-8) = 2
    c: Parallel(g-7,g2)
    c: DistanceX(g-7,g2) = 2
    c: Coincident(g7,g-4)
    c: Coincident(g8,g7)
    c: Coincident(g9,g7)
    c: Tangent(g8,g3) = 1.5708
    c: Tangent(g9,g0) = -1.5708
    c: Coincident(g9,g8)
    c: Coincident(g5,g6)
    c: DistanceY(g-10,g0) = 2
    c: DistanceY(g1,g-9) = 2
    c: Coincident(g10,g-6)
    c: Coincident(g11,g10)
    c: Coincident(g12,g10)
    c: Coincident(g13,g-5)
    c: Coincident(g14,g13)
    c: Coincident(g15,g13)
    c: Tangent(g12,g1) = -1.5708
    c: Tangent(g11,g2) = -1.5708
    c: Coincident(g11,g12)
    c: Coincident(g14,g15)
    c: Tangent(g14,g2) = -1.5708
    c: Tangent(g15,g0) = -1.5708
    c: Equal(g10,g13)
    c: Equal(g13,g7)
    c: Equal(g7,g4)
    c: Equal(g12,g6)
    c: DistanceY(g-1,g3) = 18
FEATURE [Sketcher::SketchObject] Sketch027  label="SketchButtonCarve"
  ArcFitTolerance = 0
  AttachmentOffset = pos=(10,28.6,0) rot=(0,0,1;-0.314159rad)
  AttachmentSupport = -> [YZ_Plane005]
  FullyConstrained = true
  MapMode = 5
  Placement = pos=(-4.1e-15,10,28.6) rot=(-0.506732,-0.697457,-0.506732;4.35963rad)
  Support = -> [YZ_Plane005]
  TreeRank = 0
  expr: AttachmentOffset.Base.x = <<param>>.button_offset
  expr: AttachmentOffset.Base.y = <<param>>.button_height - 2
  expr: AttachmentOffset.Rotation.Angle = <<param>>.button_angle
  expr: Constraints[12] = <<param>>.button_hole / 2 + 10
  expr: Constraints[6] = <<param>>.button_hole / 2 + 4
  sketch-geometry (4):
    g0: LineSegment StartX=0 StartY=2 StartZ=0 EndX=12.2 EndY=2 EndZ=0
    g1: ArcOfCircle CenterX=18.2 CenterY=3.09999 CenterZ=0 NormalX=0 NormalY=0 NormalZ=1 AngleXU=0 Radius=6.09999 StartAngle=3.32291 EndAngle=4.71239
    g2: LineSegment StartX=0 StartY=2 StartZ=0 EndX=0 EndY=-3 EndZ=0
    g3: LineSegment StartX=18.2 StartY=-3 StartZ=0 EndX=0 EndY=-3 EndZ=0
  constraints (13):
    c: Horizontal(g0)
    c: Coincident(g1,g0)
    c: Coincident(g2,g0)
    c: Coincident(g3,g1)
    c: Horizontal(g3)
    c: Tangent(g3,g1)
    c: DistanceX(g0,g0) = 12.2
    c: DistanceY(g2,g2) = 5
    c: Coincident(g2,g3)
    c: Vertical(g2)
    c: PointOnObject(g-1,g2)
    c: DistanceY(g2,g-1) = 3
    c: DistanceX(g3,g3) = 18.2
FEATURE [Sketcher::SketchObject] Sketch028  label="SketchTerminals"
  ArcFitTolerance = 0
  AttachmentSupport = -> [XZ_Plane005]
  FullyConstrained = true
  MapMode = 5
  Placement = pos=(0,0,0) rot=(1,0,0;1.5708rad)
  Support = -> [XZ_Plane005]
  TreeRank = 0
  expr: Constraints[17] = <<param>>.terminal_thickness
  expr: Constraints[18] = <<param>>.terminal_height
  expr: Constraints[21] = <<param>>.bottom_height
  expr: Constraints[22] = <<param>>.terminal_offset
  expr: Constraints[23] = <<param>>.terminal_seperation
  sketch-geometry (17):
    g0: LineSegment StartX=10.25 StartY=-12.9 StartZ=0 EndX=11.25 EndY=-12.9 EndZ=0
    g1: LineSegment StartX=11.25 StartY=-12.9 StartZ=0 EndX=11.25 EndY=-19.5 EndZ=0
    g2: LineSegment StartX=11.25 StartY=-19.5 StartZ=0 EndX=10.25 EndY=-19.5 EndZ=0
    g3: LineSegment StartX=10.25 StartY=-19.5 StartZ=0 EndX=10.25 EndY=-17.25 EndZ=0
    g4: LineSegment StartX=-10.25 StartY=-12.9 StartZ=0 EndX=-11.25 EndY=-12.9 EndZ=0
    g5: LineSegment StartX=-11.25 StartY=-12.9 StartZ=0 EndX=-11.25 EndY=-19.5 EndZ=0
    g6: LineSegment StartX=-11.25 StartY=-19.5 StartZ=0 EndX=-10.25 EndY=-19.5 EndZ=0
    g7: LineSegment StartX=-10.25 StartY=-19.5 StartZ=0 EndX=-10.25 EndY=-17.25 EndZ=0
    g8: Circle [constr] CenterX=0 CenterY=-24 CenterZ=0 NormalX=0 NormalY=0 NormalZ=1 AngleXU=0 Radius=3
    g9: LineSegment StartX=-10.25 StartY=-15.15 StartZ=0 EndX=-8.75 EndY=-15.15 EndZ=0
    g10: LineSegment StartX=-8.75 StartY=-15.15 StartZ=0 EndX=-8.75 EndY=-17.25 EndZ=0
    g11: LineSegment StartX=-8.75 StartY=-17.25 StartZ=0 EndX=-10.25 EndY=-17.25 EndZ=0
    g12: LineSegment StartX=-10.25 StartY=-15.15 StartZ=0 EndX=-10.25 EndY=-12.9 EndZ=0
    g13: LineSegment StartX=10.25 StartY=-15.15 StartZ=0 EndX=8.75 EndY=-15.15 EndZ=0
    g14: LineSegment StartX=8.75 StartY=-15.15 StartZ=0 EndX=8.75 EndY=-17.25 EndZ=0
    g15: LineSegment StartX=8.75 StartY=-17.25 StartZ=0 EndX=10.25 EndY=-17.25 EndZ=0
    g16: LineSegment StartX=10.25 StartY=-15.15 StartZ=0 EndX=10.25 EndY=-12.9 EndZ=0
  constraints (48):
    c: Coincident(g0,g1)
    c: Coincident(g1,g2)
    c: Coincident(g2,g3)
    c: Coincident(g16,g0)
    c: Horizontal(g0)
    c: Horizontal(g2)
    c: Vertical(g1)
    c: Vertical(g3)
    c: Coincident(g4,g5)
    c: Coincident(g5,g6)
    c: Coincident(g6,g7)
    c: Coincident(g12,g4)
    c: Horizontal(g4)
    c: Horizontal(g6)
    c: Vertical(g5)
    c: Vertical(g7)
    c: Equal(g4,g0)
    c: DistanceX(g4,g4) = 1
    c: DistanceY(g3,g16) = 6.6
    c: PointOnObject(g8,g-2)
    c: Radius(g8) = 3
    c: DistanceY(g8,g-1) = 24
    c: DistanceY(g8,g1) = 4.5
    c: DistanceX(g6,g1) = 21.5
    c: Symmetric(g4,g0,g-2)
    c: Horizontal(g9)
    c: Coincident(g10,g9)
    c: Vertical(g10)
    c: Coincident(g11,g10)
    c: Horizontal(g11)
    c: Coincident(g7,g11)
    c: Coincident(g12,g9)
    c: Tangent(g7,g12)
    c: Equal(g12,g7)
    c: Horizontal(g5,g1)
    c: DistanceY(g10,g10) = 2.1
    c: DistanceX(g9,g9) = 1.5
    c: Horizontal(g13)
    c: Coincident(g14,g13)
    c: Vertical(g14)
    c: Coincident(g15,g14)
    c: Horizontal(g15)
    c: Coincident(g3,g15)
    c: Coincident(g16,g13)
    c: Tangent(g3,g16)
    c: Equal(g16,g3)
    c: Equal(g13,g9)
    c: Equal(g14,g10)
FEATURE [Sketcher::SketchObject] Sketch029  label="SketchAccess"
  ArcFitTolerance = 0
  AttachmentOffset = pos=(0,0,-20.5) rot=(0,0,1;0rad)
  AttachmentSupport = -> [XY_Plane005]
  FullyConstrained = true
  MapMode = 5
  Placement = pos=(0,0,-20.5) rot=(0,0,1;0rad)
  Support = -> [XY_Plane005]
  TreeRank = 0
  expr: AttachmentOffset.Base.z = -<<param>>.bottom_height + <<param>>.terminal_offset - 1
  expr: Constraints[19] = <<param>>.mid_depth / 2
  expr: Constraints[22] = <<param>>.terminal_seperation + <<param>>.terminal_thickness * 2
  expr: Constraints[23] = <<param>>.terminal_depth
  sketch-geometry (12):
    g0: LineSegment StartX=-11.75 StartY=41 StartZ=0 EndX=-11.75 EndY=18.5 EndZ=0
    g1: LineSegment StartX=-11.75 StartY=18.5 StartZ=0 EndX=-9.25 EndY=18.5 EndZ=0
    g2: LineSegment StartX=-7.95 StartY=21 StartZ=0 EndX=-7.95 EndY=41 EndZ=0
    g3: LineSegment StartX=-7.95 StartY=41 StartZ=0 EndX=-11.75 EndY=41 EndZ=0
    g4: LineSegment StartX=7.95 StartY=41 StartZ=0 EndX=11.75 EndY=41 EndZ=0
    g5: LineSegment StartX=11.75 StartY=41 StartZ=0 EndX=11.75 EndY=18.5 EndZ=0
    g6: LineSegment StartX=11.75 StartY=18.5 StartZ=0 EndX=9.25 EndY=18.5 EndZ=0
    g7: LineSegment StartX=7.95 StartY=21 StartZ=0 EndX=7.95 EndY=41 EndZ=0
    g8: LineSegment StartX=9.25 StartY=18.5 StartZ=0 EndX=9.25 EndY=19.5 EndZ=0
    g9: LineSegment StartX=7.95 StartY=21 StartZ=0 EndX=9.25 EndY=19.5 EndZ=0
    g10: LineSegment StartX=-9.25 StartY=18.5 StartZ=0 EndX=-9.25 EndY=19.5 EndZ=0
    g11: LineSegment StartX=-9.25 StartY=19.5 StartZ=0 EndX=-7.95 EndY=21 EndZ=0
  constraints (35):
    c: Vertical(g0)
    c: Coincident(g0,g1)
    c: Vertical(g2)
    c: Coincident(g2,g3)
    c: Coincident(g3,g0)
    c: Horizontal(g3)
    c: Horizontal(g4)
    c: Coincident(g4,g5)
    c: Vertical(g5)
    c: Coincident(g5,g6)
    c: Horizontal(g6)
    c: Coincident(g7,g4)
    c: Vertical(g7)
    c: Equal(g3,g4)
    c: Equal(g0,g5)
    c: Horizontal(g1)
    c: Equal(g2,g7)
    c: Equal(g1,g6)
    c: Symmetric(g2,g4,g-2)
    c: DistanceY(g-1,g0) = 41
    c: DistanceX(g1,g1) = 2.5
    c: DistanceX(g0,g2) = 3.8
    c: DistanceX(g0,g5) = 23.5
    c: DistanceY(g5,g4) = 22.5
    c: DistanceY(g2,g2) = 20
    c: Coincident(g8,g6) = 23.5
    c: Vertical(g8) = 22
    c: Coincident(g9,g7)
    c: Coincident(g9,g8)
    c: Coincident(g10,g1)
    c: Coincident(g11,g10)
    c: Coincident(g11,g2)
    c: Equal(g8,g10)
    c: DistanceY(g8,g8) = 1
    c: Vertical(g10)
FEATURE [Sketcher::SketchObject] Sketch030  label="SketchFront"
  ArcFitTolerance = 0
  AttachmentOffset = pos=(0,0,41) rot=(0,0,1;0rad)
  AttachmentSupport = -> [XZ_Plane006]
  FullyConstrained = true
  MapMode = 5
  Placement = pos=(0,-41,-9.1e-15) rot=(1,0,0;1.5708rad)
  Support = -> [XZ_Plane006]
  TreeRank = 0
  expr: AttachmentOffset.Base.z = <<param>>.mid_depth / 2
  expr: Constraints[10] = <<param>>.front_width2
  expr: Constraints[11] = <<param>>.front_width2
  expr: Constraints[12] = <<param>>.front_height + 2
  expr: Constraints[22] = <<param>>.radius_big * 1.2
  expr: Constraints[27] = <<param>>.radius_big
  expr: Constraints[6] = <<param>>.radius_small
  expr: Constraints[7] = <<param>>.bottom_width
  expr: Constraints[9] = <<param>>.bottom_height
  sketch-geometry (12):
    g0: LineSegment StartX=-47.5 StartY=48 StartZ=0 EndX=47.5 EndY=48 EndZ=0
    g1: LineSegment StartX=47.5 StartY=48 StartZ=0 EndX=47.5 EndY=9.54506 EndZ=0
    g2: LineSegment StartX=36 StartY=-9.78755 StartZ=0 EndX=36 EndY=-21 EndZ=0
    g3: LineSegment StartX=33 StartY=-24 StartZ=0 EndX=-33 EndY=-24 EndZ=0
    g4: LineSegment StartX=-36 StartY=-21 StartZ=0 EndX=-36 EndY=-9.78755 EndZ=0
    g5: LineSegment StartX=-47.5 StartY=9.54506 StartZ=0 EndX=-47.5 EndY=48 EndZ=0
    g6: ArcOfCircle CenterX=-33 CenterY=-21 CenterZ=0 NormalX=0 NormalY=0 NormalZ=1 AngleXU=0 Radius=3 StartAngle=3.14159 EndAngle=4.71239
    g7: ArcOfCircle CenterX=33 CenterY=-21 CenterZ=0 NormalX=0 NormalY=0 NormalZ=1 AngleXU=0 Radius=3 StartAngle=4.71239 EndAngle=6.28319
    g8: ArcOfCircle CenterX=46 CenterY=-9.78755 CenterZ=0 NormalX=0 NormalY=0 NormalZ=1 AngleXU=0 Radius=10 StartAngle=2.06834 EndAngle=3.14159
    g9: ArcOfCircle CenterX=35.5 CenterY=9.54506 CenterZ=0 NormalX=0 NormalY=0 NormalZ=1 AngleXU=0 Radius=12 StartAngle=5.20994 EndAngle=6.28319
    g10: ArcOfCircle CenterX=-46 CenterY=-9.78755 CenterZ=0 NormalX=0 NormalY=0 NormalZ=1 AngleXU=0 Radius=10 StartAngle=0 EndAngle=1.07325
    g11: ArcOfCircle CenterX=-35.5 CenterY=9.54506 CenterZ=0 NormalX=0 NormalY=0 NormalZ=1 AngleXU=0 Radius=12 StartAngle=3.14159 EndAngle=4.21484
  constraints (30):
    c: Vertical(g2)
    c: Vertical(g4)
    c: Tangent(g4,g6) = 1.5708
    c: Tangent(g3,g6) = 1.5708
    c: Tangent(g3,g7) = 1.5708
    c: Tangent(g2,g7) = 1.5708
    c: Radius(g7) = 3
    c: DistanceX(g4,g2) = 72
    c: Symmetric(g3,g3,g-2)
    c: DistanceY(g3,g-1) = 24
    c: DistanceX(g5,g1) = 95
    c: DistanceX(g5,g1) = 95
    c: DistanceY(g3,g0) = 72
    c: Equal(g7,g6)
    c: Equal(g10,g8)
    c: Symmetric(g5,g1,g-2)
    c: Equal(g4,g2)
    c: Coincident(g8,g2)
    c: Coincident(g0,g1)
    c: Coincident(g5,g0)
    c: Symmetric(g0,g0,g-2)
    c: Equal(g9,g11)
    c: Radius(g9) = 12
    c: Tangent(g11,g5) = 1.5708
    c: Tangent(g1,g9) = 1.5708
    c: Tangent(g11,g10) = 1.5708
    c: Tangent(g8,g9) = 1.5708
    c: Radius(g8) = 10
    c: DistanceY(g8,g-1) = 1
    c: Tangent(g10,g4) = -1.5708
FEATURE [Sketcher::SketchObject] Sketch031  label="SketchRear"
  ArcFitTolerance = 0
  AttachmentOffset = pos=(0,0,-46) rot=(0,0,1;0rad)
  AttachmentSupport = -> [XZ_Plane006]
  FullyConstrained = true
  MapMode = 5
  Placement = pos=(0,46,1.02e-14) rot=(1,0,0;1.5708rad)
  Support = -> [XZ_Plane006]
  TreeRank = 0
  expr: AttachmentOffset.Base.z = -<<param>>.mid_depth / 2 - <<param>>.back_thickness
  expr: Constraints[15] = <<param>>.front_height + 2
  expr: Constraints[1] = <<param>>.radius_small
  expr: Constraints[2] = <<param>>.bottom_height
  expr: Constraints[3] = <<param>>.rear_width
  sketch-geometry (6):
    g0: LineSegment StartX=-33 StartY=-24 StartZ=0 EndX=33 EndY=-24 EndZ=0
    g1: LineSegment StartX=36 StartY=48 StartZ=0 EndX=-36 EndY=48 EndZ=0
    g2: ArcOfCircle CenterX=-33 CenterY=-21 CenterZ=0 NormalX=0 NormalY=0 NormalZ=1 AngleXU=0 Radius=3 StartAngle=3.14159 EndAngle=4.71239
    g3: ArcOfCircle CenterX=33 CenterY=-21 CenterZ=0 NormalX=0 NormalY=0 NormalZ=1 AngleXU=0 Radius=3 StartAngle=4.71239 EndAngle=6.28319
    g4: LineSegment StartX=36 StartY=-21 StartZ=0 EndX=36 EndY=48 EndZ=0
    g5: LineSegment StartX=-36 StartY=-21 StartZ=0 EndX=-36 EndY=48 EndZ=0
  constraints (19):
    c: Horizontal(g0)
    c: Radius(g3) = 3
    c: DistanceY(g0,g-1) = 24
    c: DistanceX(g2,g3) = 72
    c: Coincident(g4,g3)
    c: Vertical(g4)
    c: Coincident(g5,g2)
    c: Equal(g5,g4)
    c: Horizontal(g3,g3)
    c: Horizontal(g2,g2)
    c: Equal(g2,g3)
    c: Coincident(g0,g2)
    c: Coincident(g0,g3)
    c: Vertical(g2,g0)
    c: Vertical(g5)
    c: DistanceY(g0,g1) = 72
    c: Symmetric(g4,g5,g-2)
    c: Coincident(g4,g1)
    c: Coincident(g5,g1)
FEATURE [Part::Plane] Plane002  label="Plane"
  AttacherType = Attacher::AttachEngine3D
  AttachmentSupport = -> [XZ_Plane006]
  Length = 152
  Placement = pos=(-75,41,-75) rot=(1,0,0;1.5708rad)
  Support = -> [XZ_Plane006]
  TreeRank = 0
  Width = 150
  expr: Placement.Base.y = <<param>>.mid_depth / 2
FEATURE [Sketcher::SketchObject] Sketch032  label="SketchBack"
  ArcFitTolerance = 0
  AttachmentSupport = -> [XZ_Plane]
  FullyConstrained = true
  MapMode = 5
  Placement = pos=(0,0,0) rot=(1,0,0;1.5708rad)
  Support = -> [XZ_Plane]
  TreeRank = 0
  expr: Constraints[10] = <<param>>.rear_screw_width1
  expr: Constraints[11] = <<param>>.reart_screw_width2
  expr: Constraints[12] = <<param>>.rear_screw_height
  expr: Constraints[15] = <<param>>.rear_screw_offset
  expr: Constraints[1] = <<param>>.bottom_height
  expr: Constraints[2] = <<param>>.rear_width
  expr: Constraints[9] = <<param>>.screw_hole + 1
  sketch-geometry (6):
    g0: LineSegment [constr] StartX=36 StartY=-24 StartZ=0 EndX=-36 EndY=-24 EndZ=0
    g1: Circle CenterX=-29 CenterY=14.9 CenterZ=0 NormalX=0 NormalY=0 NormalZ=1 AngleXU=0 Radius=1.75
    g2: Circle CenterX=0 CenterY=14.9 CenterZ=0 NormalX=0 NormalY=0 NormalZ=1 AngleXU=0 Radius=1.75
    g3: Circle CenterX=29 CenterY=14.9 CenterZ=0 NormalX=0 NormalY=0 NormalZ=1 AngleXU=0 Radius=1.75
    g4: Circle CenterX=-27.5 CenterY=-16.6 CenterZ=0 NormalX=0 NormalY=0 NormalZ=1 AngleXU=0 Radius=1.75
    g5: Circle CenterX=27.5 CenterY=-16.6 CenterZ=0 NormalX=0 NormalY=0 NormalZ=1 AngleXU=0 Radius=1.75
  constraints (16):
    c: Symmetric(g0,g0,g-2)
    c: DistanceY(g0,g-1) = 24
    c: DistanceX(g0,g0) = 72
    c: Symmetric(g1,g3,g-2)
    c: Symmetric(g4,g5,g-2)
    c: Equal(g4,g1)
    c: Equal(g1,g2)
    c: Equal(g2,g3)
    c: Equal(g3,g5)
    c: Diameter(g1) = 3.5
    c: DistanceX(g1,g3) = 58
    c: DistanceX(g4,g5) = 55
    c: DistanceY(g5,g3) = 31.5
    c: Horizontal(g1,g2)
    c: PointOnObject(g2,g-2)
    c: DistanceY(g0,g5) = 7.4
FEATURE [Part::Loft] Loft
  Closed = false
  MaxDegree = 5
  Ruled = false
  Sections = -> [Sketch030,Sketch031]
  Solid = true
  TreeRank = 0
FEATURE [Part::Extrusion] Extrude
  Base = -> Sketch012
  Dir = (1,-1e-16,1e-16)
  DirMode = 2
  FaceMakerClass = Part::FaceMakerBullseye
  InnerTaperAngle = 0
  InnerTaperAngleRev = 0
  LengthFwd = 100
  LengthRev = 0
  Solid = true
  Symmetric = true
  TreeRank = 0
FEATURE [Part::MultiCommon] Common
  Shapes = -> [Extrude,Loft]
  TreeRank = 0
FEATURE [Part::FeaturePython] Slice  # WARN: FeaturePython — macro-defined, semantics opaque (R4)
  Base = -> Common
  Mode = 1
  Tolerance = 0
  Tools = -> [Plane002]
  TreeRank = 0
FEATURE [Part::FeaturePython] Slice_child0  label="Slice.0"  # WARN: FeaturePython — macro-defined, semantics opaque (R4)
  Base = -> Slice
  FilterType = 1
  Invert = false
  OverrideMaxVal = 0
  TreeRank = 0
  WindowFrom = 80
  WindowTo = 100
  items = 0
FEATURE [Part::FeaturePython] Slice_child1  label="Slice.1"  # WARN: FeaturePython — macro-defined, semantics opaque (R4)
  Base = -> Slice
  FilterType = 1
  Invert = false
  OverrideMaxVal = 0
  TreeRank = 0
  WindowFrom = 80
  WindowTo = 100
  items = 1
FEATURE [App::DocumentObjectGroup] GrExplode_Slice  label="Exploded Slice"
  ClaimAllChildren = true
  ExportMode = 1
  Group = -> [Slice_child0,Slice_child1]
  TreeRank = 0
  _GroupVersion = 1
FEATURE [App::DocumentObjectGroup] Group001  label="BaseShape"
  ClaimAllChildren = true
  ExportMode = 1
  Group = -> [Common,Sketch012,Sketch031,Sketch030,Plane002,GrExplode_Slice]
  TreeRank = 0
  _GroupVersion = 1
FEATURE [PartDesign::FeatureBase] BaseFeature
  BaseFeature = -> Slice_child1
  NewSolid = false
  Suppress = false
  TreeRank = 0
FEATURE [PartDesign::Pocket] Pocket
  BaseFeature = -> BaseFeature
  ClaimChildren = false
  Fit = 0
  FitJoin = 0
  InnerFit = 0
  InnerFitJoin = 0
  InnerTaperAngle = 0
  InnerTaperAngleRev = 0
  Length = 5
  Length2 = 100
  Midplane = true
  NewSolid = false
  Profile = -> Sketch032
  Suppress = false
  TreeRank = 0
  Type = 1
  _ProfileBasedVersion = 0
FEATURE [PartDesign::FeatureBase] BaseFeature001
  BaseFeature = -> Slice_child0
  NewSolid = false
  Suppress = false
  TreeRank = 0
FEATURE [PartDesign::Pocket] Pocket001  label="PocketBatt"
  BaseFeature = -> BaseFeature001
  ClaimChildren = false
  Fit = 0
  FitJoin = 0
  InnerFit = 0
  InnerFitJoin = 0
  InnerTaperAngle = 0
  InnerTaperAngleRev = 0
  Length = 14.6
  Length2 = 100
  NewSolid = false
  Profile = -> Sketch018
  Reversed = true
  Suppress = false
  TreeRank = 0
  Type = 0
  _ProfileBasedVersion = 0
  expr: Length = <<param>>.batt_carveout
FEATURE [PartDesign::Pad] Pad  label="PadBatt"
  BaseFeature = -> Pocket001
  ClaimChildren = false
  Direction = (1,1,1)
  Fit = 0
  FitJoin = 0
  InnerFit = 0
  InnerFitJoin = 0
  InnerTaperAngle = 0
  InnerTaperAngleRev = 0
  Length = 45
  Length2 = 100
  NewSolid = false
  Profile = -> Sketch019
  Suppress = false
  TreeRank = 0
  Type = 0
  _ProfileBasedVersion = 0
  expr: Length = <<param>>.batt_rail_length
FEATURE [PartDesign::Pocket] Pocket002  label="PocketSupport"
  BaseFeature = -> Pad
  ClaimChildren = false
  Fit = 0
  FitJoin = 0
  InnerFit = 0
  InnerFitJoin = 0
  InnerTaperAngle = 0
  InnerTaperAngleRev = 0
  Length = 5
  Length2 = 100
  NewSolid = false
  Profile = -> Sketch
  Suppress = false
  TreeRank = 0
  Type = 0
  _ProfileBasedVersion = 0
FEATURE [PartDesign::Pocket] Pocket006  label="PocketTerminal"
  BaseFeature = -> Pocket002
  ClaimChildren = false
  Fit = 0
  FitJoin = 0
  InnerFit = 0
  InnerFitJoin = 0
  InnerTaperAngle = 0
  InnerTaperAngleRev = 0
  Length = 18.5
  Length2 = 100
  NewSolid = false
  Profile = -> Sketch028
  Suppress = false
  TreeRank = 0
  Type = 0
  _ProfileBasedVersion = 0
  expr: Length = <<param>>.mid_depth / 2 - <<param>>.terminal_depth
FEATURE [PartDesign::Pocket] Pocket005  label="PocketAccess"
  BaseFeature = -> Pocket006
  ClaimChildren = false
  Fit = 0
  FitJoin = 0
  InnerFit = 0
  InnerFitJoin = 0
  InnerTaperAngle = 0
  InnerTaperAngleRev = 0
  Length = 22.5
  Length2 = 100
  NewSolid = false
  Profile = -> Sketch029
  Reversed = true
  Suppress = false
  TreeRank = 0
  Type = 0
  _ProfileBasedVersion = 0
  expr: Length = <<param>>.terminal_depth
FEATURE [Sketcher::SketchObject] Sketch033  label="SketchFace"
  ArcFitTolerance = 0
  AttachmentSupport = -> [XZ_Plane007]
  FullyConstrained = true
  MapMode = 5
  Placement = pos=(0,0,0) rot=(1,0,0;1.5708rad)
  Support = -> [XZ_Plane007]
  TreeRank = 0
  expr: Constraints[12] = <<param>>.face_radius
  expr: Constraints[21] = <<param>>.face_width1 - 0.4
  expr: Constraints[22] = <<param>>.face_width2 - 0.4
  expr: Constraints[23] = <<param>>.face_height - 0.4
  expr: Constraints[27] = <<param>>.screw_hole + 1
  expr: Constraints[28] = <<param>>.front_screw_width2 / 2
  expr: Constraints[29] = <<param>>.front_screw_width2 / 2
  expr: Constraints[30] = <<param>>.front_screw_width1 / 2
  expr: Constraints[31] = <<param>>.front_screw_width1 / 2
  expr: Constraints[32] = <<param>>.front_screw_height
  expr: Constraints[35] = <<param>>.front_screw_offset + <<param>>.face_offset
  expr: Constraints[48] = <<param>>.face_offset
  sketch-geometry (23):
    g0: LineSegment StartX=-34.3037 StartY=43.4 StartZ=0 EndX=34.3037 EndY=43.4 EndZ=0
    g1: LineSegment StartX=42.3 StartY=35.6438 StartZ=0 EndX=43.05 EndY=11.0438 EndZ=0
    g2: LineSegment StartX=35.0537 StartY=2.8 StartZ=0 EndX=-35.0537 EndY=2.8 EndZ=0
    g3: LineSegment StartX=-43.05 StartY=11.0438 StartZ=0 EndX=-42.3 EndY=35.6438 EndZ=0
    g4: ArcOfCircle CenterX=34.3037 CenterY=35.4 CenterZ=0 NormalX=0 NormalY=0 NormalZ=1 AngleXU=0 Radius=8 StartAngle=0.0304753 EndAngle=1.5708
    g5: ArcOfCircle CenterX=35.0537 CenterY=10.8 CenterZ=0 NormalX=0 NormalY=0 NormalZ=1 AngleXU=0 Radius=8 StartAngle=4.71239 EndAngle=6.31366
    g6: ArcOfCircle CenterX=-34.3037 CenterY=35.4 CenterZ=0 NormalX=0 NormalY=0 NormalZ=1 AngleXU=0 Radius=8 StartAngle=1.5708 EndAngle=3.11112
    g7: ArcOfCircle CenterX=-35.0537 CenterY=10.8 CenterZ=0 NormalX=0 NormalY=0 NormalZ=1 AngleXU=0 Radius=8 StartAngle=3.11111 EndAngle=4.71239
    g8: Circle CenterX=-36.75 CenterY=38.3 CenterZ=0 NormalX=0 NormalY=0 NormalZ=1 AngleXU=0 Radius=1.75
    g9: Circle CenterX=36.75 CenterY=38.3 CenterZ=0 NormalX=0 NormalY=0 NormalZ=1 AngleXU=0 Radius=1.75
    g10: Circle CenterX=-38 CenterY=8.3 CenterZ=0 NormalX=0 NormalY=0 NormalZ=1 AngleXU=0 Radius=1.75
    g11: Circle CenterX=38 CenterY=8.3 CenterZ=0 NormalX=0 NormalY=0 NormalZ=1 AngleXU=0 Radius=1.75
    g12: LineSegment StartX=-14 StartY=33.75 StartZ=0 EndX=14 EndY=33.75 EndZ=0
    g13: LineSegment StartX=16 StartY=31.75 StartZ=0 EndX=16 EndY=19.25 EndZ=0
    g14: LineSegment StartX=14 StartY=17.25 StartZ=0 EndX=-14 EndY=17.25 EndZ=0
    g15: LineSegment StartX=-16 StartY=19.25 StartZ=0 EndX=-16 EndY=31.75 EndZ=0
    g16: ArcOfCircle CenterX=-14 CenterY=31.75 CenterZ=0 NormalX=0 NormalY=0 NormalZ=1 AngleXU=0 Radius=2 StartAngle=1.5708 EndAngle=3.14159
    g17: ArcOfCircle CenterX=-14 CenterY=19.25 CenterZ=0 NormalX=0 NormalY=0 NormalZ=1 AngleXU=0 Radius=2 StartAngle=3.14159 EndAngle=4.71239
    g18: ArcOfCircle CenterX=14 CenterY=19.25 CenterZ=0 NormalX=0 NormalY=0 NormalZ=1 AngleXU=0 Radius=2 StartAngle=4.71239 EndAngle=6.28319
    g19: ArcOfCircle CenterX=14 CenterY=31.75 CenterZ=0 NormalX=0 NormalY=0 NormalZ=1 AngleXU=0 Radius=2 StartAngle=7e-16 EndAngle=1.5708
    g20: Circle CenterX=-31 CenterY=21.5 CenterZ=0 NormalX=0 NormalY=0 NormalZ=1 AngleXU=0 Radius=7.75
    g21: Circle CenterX=31 CenterY=25.5 CenterZ=0 NormalX=0 NormalY=0 NormalZ=1 AngleXU=0 Radius=3.6
    g22: LineSegment [constr] StartX=-69 StartY=25.5 StartZ=0 EndX=31 EndY=25.5 EndZ=0
  constraints (67):
    c: Coincident(g4,g0)
    c: Coincident(g4,g1)
    c: Coincident(g5,g1)
    c: Coincident(g5,g2)
    c: Coincident(g6,g0)
    c: Coincident(g6,g3)
    c: Coincident(g7,g3)
    c: Coincident(g7,g2)
    c: Equal(g1,g3)
    c: Equal(g4,g6)
    c: Equal(g6,g7)
    c: Equal(g7,g5)
    c: Radius(g4) = 8
    c: Tangent(g6,g3)
    c: Tangent(g7,g3)
    c: Tangent(g7,g2)
    c: Tangent(g6,g0)
    c: Tangent(g4,g0)
    c: Tangent(g4,g1)
    c: Tangent(g5,g1)
    c: Tangent(g5,g2)
    c: DistanceX(g3,g1) = 84.6
    c: DistanceX(g3,g1) = 86.1
    c: DistanceY(g2,g0) = 40.6
    c: Equal(g9,g8)
    c: Equal(g8,g10)
    c: Equal(g10,g11)
    c: Diameter(g8) = 3.5
    c: DistanceX(g10,g-1) = 38
    c: DistanceX(g-1,g11) = 38
    c: DistanceX(g-1,g9) = 36.75
    c: DistanceX(g8,g-1) = 36.75
    c: DistanceY(g11,g9) = 30
    c: Horizontal(g8,g9)
    c: Horizontal(g10,g11)
    c: DistanceY(g-1,g11) = 8.3
    c: Horizontal(g12)
    c: Horizontal(g14)
    c: Vertical(g13)
    c: Vertical(g15)
    c: Tangent(g15,g16) = 1.5708
    c: Tangent(g12,g16) = 1.5708
    c: Tangent(g15,g17) = 1.5708
    c: Tangent(g14,g17) = 1.5708
    c: Tangent(g14,g18) = 1.5708
    c: Tangent(g13,g18) = 1.5708
    c: Tangent(g12,g19) = 1.5708
    c: Tangent(g13,g19) = 1.5708
    c: DistanceY(g-1,g2) = 2.8
    c: Horizontal(g0)
    c: Symmetric(g2,g2,g-2)
    c: Diameter(g20) = 15.5
    c: Diameter(g21) = 7.2
    c: Equal(g16,g17)
    c: Equal(g17,g18)
    c: Equal(g18,g19)
    c: DistanceY(g14,g12) = 16.5
    c: DistanceX(g15,g13) = 32
    c: Radius(g19) = 2
    c: DistanceX(g20,g21) = 62
    c: DistanceX(g13,g21) = 15
    c: Symmetric(g12,g14,g22)
    c: DistanceY(g20,g22) = 4
    c: DistanceY(g-1,g22) = 25.5
    c: DistanceX(g-1,g21) = 31
    c: DistanceX(g22,g22) = 100
    c: Coincident(g22,g21)
FEATURE [PartDesign::Pad] Pad001  label="PadFace"
  ClaimChildren = false
  Direction = (1,1,1)
  Fit = 0
  FitJoin = 0
  InnerFit = 0
  InnerFitJoin = 0
  InnerTaperAngle = 0
  InnerTaperAngleRev = 0
  Length = 3
  Length2 = 100
  NewSolid = false
  Placement = pos=(0,0,0) rot=(1,0,0;1.5708rad)
  Profile = -> Sketch033
  Suppress = false
  TreeRank = 0
  Type = 0
  _ProfileBasedVersion = 0
  expr: Length = <<param>>.face_thickness
FEATURE [PartDesign::Chamfer] Chamfer001
  Angle = 45
  Base = -> Pad001 [Edge34]
  BaseFeature = -> Pad001
  ChamferType = 0
  FlipDirection = false
  NewSolid = false
  Placement = pos=(0,0,0) rot=(1,0,0;1.5708rad)
  Size = 2
  Size2 = 1
  SupportTransform = false
  Suppress = false
  TreeRank = 0
FEATURE [PartDesign::Chamfer] Chamfer002
  Angle = 45
  Base = -> Chamfer001 [Edge54,Edge56,Edge53,Edge55]
  BaseFeature = -> Chamfer001
  ChamferType = 0
  FlipDirection = false
  NewSolid = false
  Placement = pos=(0,0,0) rot=(1,0,0;1.5708rad)
  Size = 1.4
  Size2 = 1
  SupportTransform = false
  Suppress = false
  TreeRank = 0
FEATURE [Sketcher::SketchObject] Sketch034
  ArcFitTolerance = 0
  AttachmentSupport = -> [XZ_Plane008]
  FullyConstrained = true
  MapMode = 5
  Placement = pos=(0,0,0) rot=(1,0,0;1.5708rad)
  Support = -> [XZ_Plane008]
  TreeRank = 0
  sketch-geometry (6):
    g0: LineSegment StartX=-1 StartY=6.25 StartZ=0 EndX=1 EndY=6.25 EndZ=0
    g1: LineSegment StartX=1 StartY=6.25 StartZ=0 EndX=1 EndY=7.75 EndZ=0
    g2: LineSegment StartX=1 StartY=7.75 StartZ=0 EndX=0.3 EndY=7.75 EndZ=0
    g3: LineSegment StartX=0.3 StartY=7.75 StartZ=0 EndX=0.3 EndY=8.75 EndZ=0
    g4: LineSegment StartX=0.3 StartY=8.75 StartZ=0 EndX=-1 EndY=8.75 EndZ=0
    g5: LineSegment StartX=-1 StartY=8.75 StartZ=0 EndX=-1 EndY=6.25 EndZ=0
  constraints (17):
    c: Coincident(g0,g1)
    c: Vertical(g1)
    c: Coincident(g1,g2)
    c: Horizontal(g2)
    c: Coincident(g2,g3)
    c: Vertical(g3)
    c: Coincident(g3,g4)
    c: Horizontal(g4)
    c: Coincident(g4,g5)
    c: Coincident(g5,g0)
    c: Vertical(g5)
    c: DistanceX(g0,g0) = 2
    c: DistanceY(g3,g3) = 1
    c: DistanceX(g4,g4) = 1.3
    c: Symmetric(g0,g0,g-2)
    c: DistanceY(g-1,g0) = 6.25
    c: DistanceY(g5,g5) = 2.5
FEATURE [PartDesign::Revolution] Revolution001
  Angle = 360
  Axis = (1,0,0)
  Base = (0,0,0)
  ClaimChildren = false
  Fit = 0
  FitJoin = 0
  InnerFit = 0
  InnerFitJoin = 0
  NewSolid = false
  Placement = pos=(0,0,0) rot=(1,0,0;1.5708rad)
  Profile = -> Sketch034
  ReferenceAxis = -> X_Axis008
  Suppress = false
  TreeRank = 0
  _ProfileBasedVersion = 0
FEATURE [PartDesign::Body] Body006  label="BodyRing"
  AutoGroupSolids = false
  ClaimAllChildren = false
  ExportMode = 0
  Group = -> [Sketch034,Revolution001]
  Origin = -> Origin008
  Tip = -> Revolution001
  TreeRank = 0
  _ExportChildren = -> [Revolution001]
  _GroupVersion = 1
FEATURE [Part::Box] Box  label="Cube"
  AttacherType = Attacher::AttachEngine3D
  Height = 18
  Length = 18
  Placement = pos=(-9,-0.25,-9) rot=(0,0,1;0rad)
  TreeRank = 0
  Width = 0.5
FEATURE [Part::FeaturePython] Slice001  # WARN: FeaturePython — macro-defined, semantics opaque (R4)
  Base = -> Body006
  Mode = 1
  Tolerance = 0
  Tools = -> [Box]
  TreeRank = 0
FEATURE [Part::FeaturePython] Slice001_child1  label="Slice001.1"  # WARN: FeaturePython — macro-defined, semantics opaque (R4)
  Base = -> Slice001
  FilterType = 1
  Invert = false
  OverrideMaxVal = 0
  TreeRank = 0
  WindowFrom = 80
  WindowTo = 100
  items = 1
FEATURE [Part::FeaturePython] Slice001_child2  label="Slice001.2"  # WARN: FeaturePython — macro-defined, semantics opaque (R4)
  Base = -> Slice001
  FilterType = 1
  Invert = false
  OverrideMaxVal = 0
  TreeRank = 0
  WindowFrom = 80
  WindowTo = 100
  items = 2
FEATURE [App::DocumentObjectGroup] GrExplode_Slice001  label="Exploded SliceRing"
  ClaimAllChildren = true
  ExportMode = 1
  Group = -> [Slice001_child1,Slice001_child2]
  TreeRank = 0
  _GroupVersion = 1
FEATURE [Sketcher::SketchObject] Sketch035
  ArcFitTolerance = 0
  AttachmentOffset = pos=(0,0,1.5) rot=(1,0,0;0rad)
  AttachmentSupport = -> [XZ_Plane007]
  ExternalGeometry = -> [Sketch033]
  FullyConstrained = true
  MapMode = 5
  Placement = pos=(0,-1.5,-3e-16) rot=(1,0,0;1.5708rad)
  Support = -> [XZ_Plane007]
  TreeRank = 0
  expr: AttachmentOffset.Base.z = <<param>>.face_thickness - 1.5
  sketch-geometry (1):
    g0: Circle CenterX=-31 CenterY=21.5 CenterZ=0 NormalX=0 NormalY=0 NormalZ=1 AngleXU=0 Radius=9
  constraints (2):
    c: Coincident(g0,g-3)
    c: Diameter(g0) = 18
FEATURE [PartDesign::Pocket] Pocket008
  BaseFeature = -> Chamfer002
  ClaimChildren = false
  Fit = 0
  FitJoin = 0
  InnerFit = 0
  InnerFitJoin = 0
  InnerTaperAngle = 0
  InnerTaperAngleRev = 0
  Length = 1.5
  Length2 = 100
  NewSolid = false
  Placement = pos=(0,0,0) rot=(1,0,0;1.5708rad)
  Profile = -> Sketch035
  Reversed = true
  Suppress = false
  TreeRank = 0
  Type = 1
  _ProfileBasedVersion = 0
FEATURE [Sketcher::SketchObject] Sketch036
  ArcFitTolerance = 0
  AttachmentSupport = -> [XZ_Plane007]
  ExternalGeometry = -> [Sketch033]
  FullyConstrained = true
  MapMode = 5
  Placement = pos=(0,0,0) rot=(1,0,0;1.5708rad)
  Support = -> [XZ_Plane007]
  TreeRank = 0
  sketch-geometry (5):
    g0: ArcOfCircle CenterX=30 CenterY=19.5 CenterZ=0 NormalX=0 NormalY=0 NormalZ=1 AngleXU=0 Radius=0.75 StartAngle=1.5708 EndAngle=4.71239
    g1: ArcOfCircle CenterX=32 CenterY=19.5 CenterZ=0 NormalX=0 NormalY=0 NormalZ=1 AngleXU=0 Radius=0.75 StartAngle=4.71239 EndAngle=7.85398
    g2: LineSegment StartX=30 StartY=18.75 StartZ=0 EndX=32 EndY=18.75 EndZ=0
    g3: LineSegment StartX=30 StartY=20.25 StartZ=0 EndX=32 EndY=20.25 EndZ=0
    g4: LineSegment [constr] StartX=31 StartY=25.5 StartZ=0 EndX=31 EndY=16.5 EndZ=0
  constraints (12):
    c: Tangent(g0,g3) = 1.5708
    c: Tangent(g0,g2) = -1.5708
    c: Tangent(g2,g1) = -1.5708
    c: Tangent(g3,g1) = 1.5708
    c: Horizontal(g2)
    c: Equal(g0,g1)
    c: DistanceY(g1,g-3) = 6
    c: DistanceY(g1,g1) = 1.5
    c: DistanceX(g0,g1) = 2
    c: Coincident(g4,g-3)
    c: Symmetric(g0,g1,g4)
    c: DistanceY(g4,g4) = 9
FEATURE [PartDesign::Pocket] Pocket009
  BaseFeature = -> Pocket008
  ClaimChildren = false
  Fit = 0
  FitJoin = 0
  InnerFit = 0
  InnerFitJoin = 0
  InnerTaperAngle = 0
  InnerTaperAngleRev = 0
  Length = 1
  Length2 = 100
  NewSolid = false
  Placement = pos=(0,0,0) rot=(1,0,0;1.5708rad)
  Profile = -> Sketch036
  Reversed = true
  Suppress = false
  TreeRank = 0
  Type = 0
  _ProfileBasedVersion = 0
FEATURE [PartDesign::Fillet] Fillet
  Base = -> Pocket [Edge63,Edge30]
  BaseFeature = -> Pocket
  NewSolid = false
  Radius = 10
  SupportTransform = false
  Suppress = false
  TreeRank = 0
  expr: Radius = <<param>>.radius_big
FEATURE [PartDesign::Fillet] Fillet004
  Base = -> Fillet [Edge4]
  BaseFeature = -> Fillet
  NewSolid = false
  Radius = 2.9
  SupportTransform = false
  Suppress = false
  TreeRank = 0
FEATURE [PartDesign::Chamfer] Chamfer
  Angle = 45
  Base = -> Fillet004 [Edge9,Edge10,Edge11,Edge25,Edge26]
  BaseFeature = -> Fillet004
  ChamferType = 0
  FlipDirection = false
  NewSolid = false
  Size = 1.4
  Size2 = 1
  SupportTransform = false
  Suppress = false
  TreeRank = 0
FEATURE [PartDesign::Body] Body  label="BodyBack"
  AutoGroupSolids = false
  BaseFeature = -> Slice_child1
  ClaimAllChildren = false
  ExportMode = 0
  Group = -> [BaseFeature,Sketch032,Pocket,Fillet,Fillet004,Chamfer]
  Origin = -> Origin
  Tip = -> Chamfer
  TreeRank = 0
  _ExportChildren = -> [BaseFeature,Pocket,Fillet,Fillet004,Chamfer]
  _GroupVersion = 1
FEATURE [Sketcher::SketchObject] Sketch037
  ArcFitTolerance = 0
  AttachmentOffset = pos=(0,0,-41) rot=(0,0,1;0rad)
  AttachmentSupport = -> [XZ_Plane005]
  FullyConstrained = true
  MapMode = 5
  Placement = pos=(0,41,9.1e-15) rot=(1,0,0;1.5708rad)
  Support = -> [XZ_Plane005]
  TreeRank = 0
  expr: AttachmentOffset.Base.z = -<<param>>.mid_depth / 2
  expr: Constraints[20] = <<param>>.reart_screw_width2
  expr: Constraints[23] = <<param>>.screw_hole / 2
  expr: Constraints[24] = <<param>>.rear_screw_offset
  expr: Constraints[2] = <<param>>.bottom_height
  sketch-geometry (9):
    g0: Circle [constr] CenterX=0 CenterY=-24 CenterZ=0 NormalX=0 NormalY=0 NormalZ=1 AngleXU=0 Radius=3
    g1: LineSegment StartX=4.5 StartY=-22.8 StartZ=0 EndX=4.5 EndY=-24 EndZ=0
    g2: LineSegment StartX=4.5 StartY=-24 StartZ=0 EndX=11.5 EndY=-24 EndZ=0
    g3: LineSegment StartX=11.5 StartY=-24 StartZ=0 EndX=11.5 EndY=-22.8 EndZ=0
    g4: ArcOfCircle CenterX=5.5 CenterY=-22.8 CenterZ=0 NormalX=0 NormalY=0 NormalZ=1 AngleXU=0 Radius=1 StartAngle=1.5708 EndAngle=3.14159
    g5: ArcOfCircle CenterX=10.5 CenterY=-22.8 CenterZ=0 NormalX=0 NormalY=0 NormalZ=1 AngleXU=0 Radius=1 StartAngle=-9e-16 EndAngle=1.5708
    g6: LineSegment StartX=5.5 StartY=-21.8 StartZ=0 EndX=10.5 EndY=-21.8 EndZ=0
    g7: Circle CenterX=-27.5 CenterY=-16.6 CenterZ=0 NormalX=0 NormalY=0 NormalZ=1 AngleXU=0 Radius=1.25
    g8: Circle CenterX=27.5 CenterY=-16.6 CenterZ=0 NormalX=0 NormalY=0 NormalZ=1 AngleXU=0 Radius=1.25
  constraints (25):
    c: PointOnObject(g0,g-2)
    c: Radius(g0) = 3
    c: DistanceY(g0,g-1) = 24
    c: Vertical(g1)
    c: Coincident(g1,g2)
    c: Horizontal(g2)
    c: Coincident(g2,g3)
    c: Coincident(g5,g3)
    c: Horizontal(g6)
    c: Vertical(g3)
    c: Horizontal(g0,g1)
    c: DistanceX(g0,g1) = 4.5
    c: Equal(g3,g1)
    c: Equal(g4,g5)
    c: Radius(g5) = 1
    c: Tangent(g6,g4) = 1.5708
    c: Tangent(g6,g5) = 1.5708
    c: Tangent(g4,g1) = -1.5708
    c: DistanceY(g2,g5) = 2.2
    c: DistanceX(g1,g2) = 7
    c: DistanceX(g7,g8) = 55
    c: Symmetric(g7,g8,g-2)
    c: Equal(g7,g8)
    c: Radius(g7) = 1.25
    c: DistanceY(g0,g7) = 7.4
FEATURE [PartDesign::Pocket] Pocket010  label="PocketKey"
  BaseFeature = -> Pocket005
  ClaimChildren = false
  Fit = 0
  FitJoin = 0
  InnerFit = 0
  InnerFitJoin = 0
  InnerTaperAngle = 0
  InnerTaperAngleRev = 0
  Length = 0
  Length2 = 100
  Midplane = true
  NewSolid = false
  Profile = -> Sketch037
  Suppress = false
  TreeRank = 0
  Type = 3
  UpToFace = -> Pocket005 [Face26]
  _ProfileBasedVersion = 0
FEATURE [PartDesign::SubtractiveLoft] SubtractiveLoft
  BaseFeature = -> Pocket010
  ClaimChildren = false
  Closed = false
  Fit = 0
  FitJoin = 0
  InnerFit = 0
  InnerFitJoin = 0
  NewSolid = false
  Profile = -> Sketch022
  Ruled = true
  Sections = -> [Sketch025,Sketch023]
  Suppress = false
  TreeRank = 0
  _ProfileBasedVersion = 0
FEATURE [PartDesign::Revolution] Revolution  label="RevolutionButton"
  Angle = 360
  Axis = (-1e-16,0.309017,0.951057)
  Base = (-4.6e-15,10,30.6)
  BaseFeature = -> SubtractiveLoft
  ClaimChildren = false
  Fit = 0
  FitJoin = 0
  InnerFit = 0
  InnerFitJoin = 0
  NewSolid = false
  Profile = -> Sketch021
  ReferenceAxis = -> Sketch021 [V_Axis]
  Reversed = true
  Suppress = false
  TreeRank = 0
  _ProfileBasedVersion = 0
FEATURE [PartDesign::Pocket] Pocket007  label="PocketButton"
  BaseFeature = -> Revolution
  ClaimChildren = false
  Fit = 0
  FitJoin = 0
  InnerFit = 0
  InnerFitJoin = 0
  InnerTaperAngle = 0
  InnerTaperAngleRev = 0
  Length = 14
  Length2 = 100
  NewSolid = false
  Profile = -> Sketch008
  Reversed = true
  Suppress = false
  TreeRank = 0
  Type = 0
  _ProfileBasedVersion = 0
FEATURE [PartDesign::Groove] Groove  label="GrooveButton"
  Angle = 360
  Axis = (-1e-16,0.309017,0.951057)
  Base = (-4.1e-15,10,28.6)
  BaseFeature = -> Pocket007
  ClaimChildren = false
  Fit = 0
  FitJoin = 0
  InnerFit = 0
  InnerFitJoin = 0
  NewSolid = false
  Profile = -> Sketch027
  ReferenceAxis = -> Sketch027 [V_Axis]
  Suppress = false
  TreeRank = 0
  _ProfileBasedVersion = 0
FEATURE [PartDesign::Pocket] Pocket004  label="PocketFrontScrews"
  BaseFeature = -> Groove
  ClaimChildren = false
  Fit = 0
  FitJoin = 0
  InnerFit = 0
  InnerFitJoin = 0
  InnerTaperAngle = 0
  InnerTaperAngleRev = 0
  Length = 5
  Length2 = 100
  NewSolid = false
  Profile = -> Sketch026
  Suppress = false
  TreeRank = 0
  Type = 0
  _ProfileBasedVersion = 0
FEATURE [PartDesign::Pocket] Pocket003  label="PocketFace"
  BaseFeature = -> Pocket004
  ClaimChildren = false
  Fit = 0
  FitJoin = 0
  InnerFit = 0
  InnerFitJoin = 0
  InnerTaperAngle = 0
  InnerTaperAngleRev = 0
  Length = 6
  Length2 = 100
  NewSolid = false
  Profile = -> Sketch024
  Reversed = true
  Suppress = false
  TreeRank = 0
  Type = 0
  _ProfileBasedVersion = 0
  expr: Length = <<param>>.face_thickness * 2
FEATURE [PartDesign::Fillet] Fillet005  label="FilletBig"
  Base = -> Pocket003 [Edge122,Edge198]
  BaseFeature = -> Pocket003
  NewSolid = false
  Radius = 10
  SupportTransform = false
  Suppress = false
  TreeRank = 0
  expr: Radius = <<param>>.radius_big
FEATURE [PartDesign::Fillet] Fillet006  label="FilletFront"
  Base = -> Fillet005 [Edge5]
  BaseFeature = -> Fillet005
  NewSolid = false
  Radius = 2
  SupportTransform = false
  Suppress = false
  TreeRank = 0
FEATURE [PartDesign::Fillet] Fillet007  label="FilletFace"
  Base = -> Fillet006 [Edge7]
  BaseFeature = -> Fillet006
  NewSolid = false
  Radius = 2
  SupportTransform = false
  Suppress = false
  TreeRank = 0
FEATURE [PartDesign::Fillet] Fillet008  label="FilletButton"
  Base = -> Fillet007 [Edge95]
  BaseFeature = -> Fillet007
  NewSolid = false
  Radius = 10
  SupportTransform = false
  Suppress = false
  TreeRank = 0
FEATURE [PartDesign::Body] Body004  label="BodyCase"
  AutoGroupSolids = false
  BaseFeature = -> Slice_child0
  ClaimAllChildren = false
  ExportMode = 0
  Group = -> [BaseFeature001,Sketch008,Sketch029,Sketch018,Sketch019,Sketch021,Sketch022,Sketch023,Sketch024,Sketch025,Sketch026,Sketch027,Sketch028,Sketch,Pocket001,Pad,Pocket002,Pocket006,Pocket005,Pocket010,SubtractiveLoft,Revolution,Pocket007,Groove,Pocket004,Pocket003,Fillet005,Fillet006,Fillet007,Fillet008,Sketch037]
  Origin = -> Origin005
  Tip = -> Fillet008
  TreeRank = 0
  _ExportChildren = -> [BaseFeature001,Pocket001,Pad,Pocket002,Pocket006,Pocket005,Pocket010,SubtractiveLoft,Revolution,Pocket007,Groove,Pocket004,Pocket003,Fillet005,Fillet006,Fillet007,Fillet008]
  _GroupVersion = 1
FEATURE [Mesh::Feature] Mesh  label="BodyBack (Meshed)"
  TreeRank = 0
FEATURE [Mesh::Feature] Mesh004  label="BodyCase (Meshed)"
  TreeRank = 0
FEATURE [Part::Part2DObjectPython] ShapeString  # Draft 2D object (typed FeaturePython)
  AttachmentOffset = pos=(7,7,0) rot=(0,0,1;0rad)
  AttachmentSupport = -> [XZ_Plane007]
  FontFile = <path>
  MapMode = 5
  Placement = pos=(7,-1.6e-15,7) rot=(1,0,0;1.5708rad)
  Size = 5
  String = KSGER
  Support = -> [XZ_Plane007]
  Tracking = 0
  TreeRank = 1
FEATURE [PartDesign::SubShapeBinder] Import  label="Import(ShapeString)"
  BindCopyOnChange = 0
  BindMode = 0
  ClaimChildren = false
  Context = -> Part [Body005.Import.]
  FillStyle = 0
  Fuse = false
  MakeFace = false
  OffsetFill = false
  OffsetIntersection = false
  OffsetJoinType = 0
  OffsetOpenResult = false
  PartialLoad = false
  Relative = true
  Support = -> [ShapeString]
  TreeRank = 2
  _Version = 8
FEATURE [PartDesign::Pocket] Pocket011
  BaseFeature = -> Pocket009
  ClaimChildren = false
  Fit = 0
  FitJoin = 0
  InnerFit = 0
  InnerFitJoin = 0
  InnerTaperAngle = 0
  InnerTaperAngleRev = 0
  Length = 10
  Length2 = 100
  Linearize = true
  Midplane = true
  NewSolid = false
  Placement = pos=(0,0,0) rot=(1,0,0;1.5708rad)
  Profile = -> Import
  Suppress = false
  TreeRank = 3
  Type = 0
  _ProfileBasedVersion = 1
FEATURE [PartDesign::Body] Body005  label="BodyKSGER"
  AutoGroupSolids = false
  ClaimAllChildren = false
  ExportMode = 0
  Group = -> [Sketch033,Pad001,Chamfer001,Chamfer002,Sketch035,Pocket008,Sketch036,Pocket009,Import,Pocket011]
  Origin = -> Origin007
  Tip = -> Pocket011
  TreeRank = 0
  _ExportChildren = -> [Pad001,Chamfer001,Chamfer002,Pocket008,Pocket009,Pocket011]
  _GroupVersion = 1
FEATURE [Mesh::Feature] Mesh005  label="BodyKSGER (Meshed)"
  TreeRank = 4
FEATURE [Mesh::Feature] Mesh006  label="SliceRing (Meshed)"
  TreeRank = 5
FEATURE [App::DocumentObjectGroup] Group  label="Mesh"
  ClaimAllChildren = true
  ExportMode = 1
  Group = -> [Mesh,Mesh004,Mesh005,Mesh006]
  TreeRank = 0
  _GroupVersion = 1
FEATURE [App::Part] Part
  ClaimAllChildren = false
  ExportMode = 1
  Group = -> [Extrude,Plane002,Common,Sketch012,Loft,Slice_child1,Slice_child0,Slice,GrExplode_Slice,Sketch030,Sketch031,Group001,Spreadsheet,Body,Body004,Body005,Group,Mesh,Mesh004,Mesh005,Mesh006]
  Origin = -> Origin006
  TreeRank = 0
  _ExportChildren = -> [Group001,Spreadsheet,Body,Body004,Body005,Group]
  _GroupVersion = 1
note: 1 file-system path scrubbed to <path> (originals preserved in the JSON sidecar)
